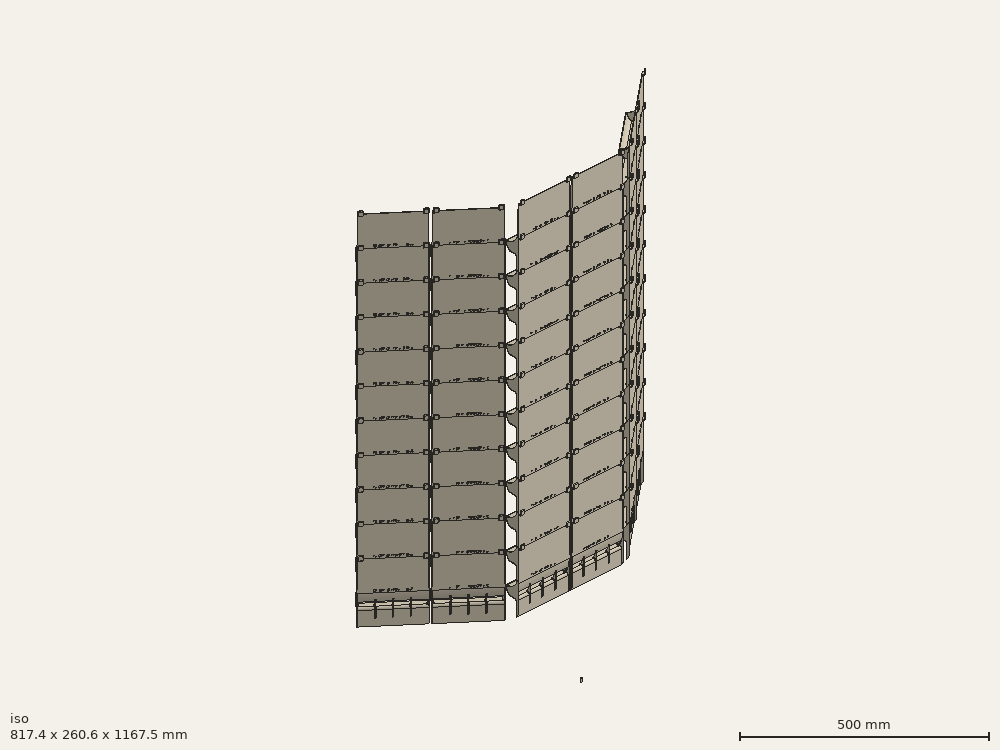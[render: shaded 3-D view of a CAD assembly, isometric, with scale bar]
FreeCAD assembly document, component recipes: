
FREECAD ASSEMBLY — COMPONENT RECIPES ("composit_stand12")

This assembly document has 30 components, labeled P0..P29 below (a component is one placed body or linked part). 28 of them carry a construction recipe — the FreeCAD feature program that regenerates the part from scratch, quoted from this document or its linked companion documents; the rest are supplied as boundary geometry only. No exploded tour is included for this assembly.
COMPONENT P0 — recipe-attached ("Body003", modeled in this document).
Construction recipe (the document's own serialized feature program — sketch geometry with constraints, then the solid features built on it; lengths are millimeters unless a unit is written):

FEATURE [PartDesign::SubShapeBinder] Binder007
  BindCopyOnChange = 0
  BindMode = 0
  ClaimChildren = false
  Context = -> Body003 [Binder007.]
  Fuse = false
  MakeFace = true
  OffsetFill = false
  OffsetIntersection = false
  OffsetJoinType = 0
  OffsetOpenResult = false
  PartialLoad = false
  Relative = true
  Support = -> [Sketch003[Edge1]]
  _Version = 2
FEATURE [Sketcher::SketchObject] Sketch016
  AttachmentSupport = -> [YZ_Plane003]
  ExternalGeometry = -> [Binder007]
  FullyConstrained = true
  MapMode = 5
  Placement = pos=(0,0,0) rot=(0.57735,0.57735,0.57735;2.0944rad)
  sketch-geometry (3):
    g0: ArcOfCircle CenterX=2.5 CenterY=3.01366 CenterZ=0 NormalX=0 NormalY=0 NormalZ=1 AngleXU=0 Radius=2.5 StartAngle=3.14159 EndAngle=4.89818
    g1: LineSegment StartX=2.9618 StartY=0.556683 StartZ=0 EndX=2.5 EndY=3.01366 EndZ=0
    g2: LineSegment StartX=2.5 StartY=3.01366 StartZ=0 EndX=0 EndY=3.01366 EndZ=0
  constraints (9):
    c: PointOnObject(g0,g-3)
    c: PointOnObject(g0,g-2)
    c: Coincident(g0,g1)
    c: Coincident(g1,g0)
    c: Coincident(g1,g2)
    c: Coincident(g2,g0)
    c: Perpendicular(g-3,g1)
    c: Perpendicular(g-2,g2)
    c: Radius(g0) = 2.5
FEATURE [PartDesign::Pad] Pad007
  Direction = (1,0,0)
  Length = 50
  Length2 = 10
  Midplane = true
  Placement = pos=(0,0,0) rot=(0.57735,0.57735,0.57735;2.0944rad)
  Profile = -> Sketch016
  ReferenceAxis = -> Sketch016 [N_Axis]
  Suppressed = false
  Type = 0
FEATURE [Sketcher::SketchObject] Sketch017
  AttachmentSupport = -> [XZ_Plane003]
  ExternalGeometry = -> [Sketch016]
  FullyConstrained = true
  MapMode = 5
  Placement = pos=(0,0,0) rot=(1,0,0;1.5708rad)
  expr: Constraints[8] = <<Pad007>>.Length
  sketch-geometry (4):
    g0: LineSegment StartX=-25 StartY=3.01366 StartZ=0 EndX=25 EndY=3.01366 EndZ=0
    g1: ArcOfCircle CenterX=23 CenterY=3.01366 CenterZ=0 NormalX=0 NormalY=0 NormalZ=1 AngleXU=0 Radius=2 StartAngle=0 EndAngle=1.5708
    g2: ArcOfCircle CenterX=-23 CenterY=3.01366 CenterZ=0 NormalX=0 NormalY=0 NormalZ=1 AngleXU=0 Radius=2 StartAngle=1.5708 EndAngle=3.14159
    g3: LineSegment StartX=-23 StartY=5.01366 StartZ=0 EndX=23 EndY=5.01366 EndZ=0
  constraints (11):
    c: PointOnObject(g1,g0)
    c: Coincident(g1,g0)
    c: PointOnObject(g2,g0)
    c: Coincident(g2,g0)
    c: Horizontal(g3)
    c: Tangent(g3,g2) = 1.5708
    c: Tangent(g3,g1) = 1.5708
    c: Symmetric(g0,g0,g-2)
    c: DistanceX(g0,g0) = 50
    c: Radius(g1) = 2
    c: PointOnObject(g-3,g0)
FEATURE [PartDesign::Pad] Pad008
  BaseFeature = -> Pad007
  Direction = (0,-1,2e-16)
  Length = 2
  Length2 = 10
  Placement = pos=(0,0,0) rot=(0.57735,0.57735,0.57735;2.0944rad)
  Profile = -> Sketch017
  ReferenceAxis = -> Sketch017 [N_Axis]
  Reversed = true
  Suppressed = false
  Type = 0
FEATURE [Sketcher::SketchObject] Sketch018
  AttachmentSupport = -> [Sketch016]
  FullyConstrained = true
  MapMode = 7
  Placement = pos=(0,2.9618,0.556683) rot=(1,0,0;0.185787rad)
  expr: Constraints[6] = <<Pad007>>.Length
  sketch-geometry (4):
    g0: ArcOfCircle CenterX=22 CenterY=0 CenterZ=0 NormalX=0 NormalY=0 NormalZ=1 AngleXU=0 Radius=3 StartAngle=0 EndAngle=1.5708
    g1: ArcOfCircle CenterX=-22 CenterY=0 CenterZ=0 NormalX=0 NormalY=0 NormalZ=1 AngleXU=0 Radius=3 StartAngle=1.5708 EndAngle=3.14159
    g2: LineSegment StartX=-22 StartY=3 StartZ=0 EndX=22 EndY=3 EndZ=0
    g3: LineSegment StartX=-25 StartY=4e-16 StartZ=0 EndX=25 EndY=0 EndZ=0
  constraints (11):
    c: PointOnObject(g0,g-1)
    c: PointOnObject(g0,g-1)
    c: PointOnObject(g1,g-1)
    c: Coincident(g3,g1)
    c: Coincident(g3,g0)
    c: Symmetric(g1,g0,g-2)
    c: DistanceX(g3,g3) = 50
    c: Horizontal(g2)
    c: Tangent(g2,g0) = 1.5708
    c: Tangent(g2,g1) = 1.5708
    c: Radius(g0) = 3
FEATURE [PartDesign::Pad] Pad009
  BaseFeature = -> Pad008
  Direction = (0,-0.18472,0.982791)
  Length = 2
  Length2 = 10
  Placement = pos=(0,0,0) rot=(0.57735,0.57735,0.57735;2.0944rad)
  Profile = -> Sketch018
  ReferenceAxis = -> Sketch018 [N_Axis]
  Suppressed = false
  Type = 0
FEATURE [PartDesign::Body] Body003
  Group = -> [Binder007,Sketch016,Pad007,Sketch017,Pad008,Sketch018,Pad009]
  Origin = -> Origin003
  Tip = -> Pad009
COMPONENT P1 — recipe-attached ("dropper_fix_composit", modeled in this document).
Construction recipe (the document's own serialized feature program — sketch geometry with constraints, then the solid features built on it; lengths are millimeters unless a unit is written):

FEATURE [PartDesign::SubShapeBinder] Binder008
  BindCopyOnChange = 0
  BindMode = 0
  ClaimChildren = true
  Context = -> Body004 [Binder008.]
  Fuse = false
  MakeFace = true
  OffsetFill = false
  OffsetIntersection = false
  OffsetJoinType = 0
  OffsetOpenResult = false
  PartialLoad = false
  Relative = true
  Support = -> [Connect002]
  _Version = 2
FEATURE [PartDesign::FeaturePython] BaseBend001  # WARN: FeaturePython — macro-defined, semantics opaque (R4)
  BendSide = 0
  BendSketch = -> Binder008
  MidPlane = false
  Reverse = false
  Suppressed = false
  length = 100
  radius = 0.1
  thickness = 0.3
FEATURE [PartDesign::FeaturePython] Extend001  # WARN: FeaturePython — macro-defined, semantics opaque (R4)
  BaseFeature = -> BaseBend001
  Offset = 0.02
  Refine = true
  Suppressed = false
  UseSubtraction = false
  baseObject = -> BaseBend001 [Face1]
  gap1 = 0
  gap2 = 0
  length = 0
FEATURE [PartDesign::FeaturePython] Bend001  # WARN: FeaturePython — macro-defined, semantics opaque (R4)
  AutoMiter = false
  BaseFeature = -> Extend001
  BendType = 1
  LengthList = [20]
  LengthSpec = 1
  ReliefFactor = 0.7
  Suppressed = false
  UseReliefFactor = false
  angle = 90
  baseObject = -> Extend001 [Edge4,Edge7,Edge14,Edge16,Edge17,Edge18]
  bendAList = [90]
  extend1 = 0
  extend2 = 0
  gap1 = 0
  gap2 = 0
  invert = false
  kfactor = 0.5
  length = 20
  maxExtendDist = 5
  minGap = 0.2
  minReliefGap = 1
  miterangle1 = 0
  miterangle2 = 0
  offset = 0
  radius = 0.1
  reliefType = 0
  reliefd = 1
  reliefw = 0.8
  sketchflip = false
  sketchinvert = false
  unfold = false
  expr: radius = BaseBend001.radius
FEATURE [PartDesign::Boolean] Boolean003
  BaseFeature = -> Bend001
  Group = -> [Fusion004]
  Suppressed = false
  Type = 1
  UsePlacement = true
FEATURE [PartDesign::Boolean] Boolean004
  BaseFeature = -> Boolean003
  Group = -> [Compound005]
  Refine = true
  Suppressed = false
  Type = 0
  UsePlacement = true
FEATURE [PartDesign::CoordinateSystem] Local_CS002  label="dropper_fix_composit_LCS"
  AttacherType = Attacher::AttachEngine3D
  AttachmentSupport = -> [XY_Plane004]
  MapMode = 5
FEATURE [PartDesign::CoordinateSystem] Local_CS003  label="dropper_fix_composit_dropper_fix_PP1_LCS"
  AttacherType = Attacher::AttachEngine3D
  AttachmentOffset = pos=(0,0,3) rot=(0,0,1;0rad)
  AttachmentSupport = -> [XY_Plane004]
  MapMode = 5
  Placement = pos=(0,0,3) rot=(0,0,1;0rad)
FEATURE [PartDesign::CoordinateSystem] Local_CS031  label="dropper_fix_composit_dropper_fix_PP2_LCS"
  AttacherType = Attacher::AttachEngine3D
  AttachmentOffset = pos=(291.934,105.683,3) rot=(0,0,1;0.694667rad)
  AttachmentSupport = -> [XY_Plane004]
  MapMode = 5
  Placement = pos=(291.934,105.683,3) rot=(0,0,1;0.694667rad)
  expr: AttachmentOffset = <<dropper_fix_composit_dropper_fix_PP1_LCS>>.AttachmentOffset * <<Placment036>>.Placement
FEATURE [PartDesign::CoordinateSystem] Local_CS032  label="dropper_fix_composit_dropper_fix_PP3_LCS"
  AttacherType = Attacher::AttachEngine3D
  AttachmentOffset = pos=(-291.934,105.683,3) rot=(0,0,1;5.58852rad)
  AttachmentSupport = -> [XY_Plane004]
  MapMode = 5
  Placement = pos=(-291.934,105.683,3) rot=(0,0,1;5.58852rad)
  expr: AttachmentOffset = <<dropper_fix_composit_dropper_fix_PP1_LCS>>.AttachmentOffset * <<Placment037>>.Placement
FEATURE [PartDesign::CoordinateSystem] Local_CS034  label="dropper_fix_composit_door_jumb_LCS"
  AttacherType = Attacher::AttachEngine3D
  AttachmentOffset = pos=(0,193,0) rot=(0,1,0;3.14159rad)
  AttachmentSupport = -> [XY_Plane004]
  MapMode = 5
  Placement = pos=(0,193,0) rot=(0,1,0;3.14159rad)
  expr: AttachmentOffset = <<door_jumb_placement>>.Placement
FEATURE [PartDesign::Boolean] Boolean006
  BaseFeature = -> Boolean004
  Group = -> [Fusion006]
  Suppressed = false
  Type = 1
  UsePlacement = true
FEATURE [PartDesign::Body] Body004  label="dropper_fix_composit"
  Group = -> [Binder008,BaseBend001,Extend001,Bend001,Boolean003,Boolean004,Boolean006,Local_CS002,Local_CS003,Local_CS031,Local_CS032,Local_CS034]
  Origin = -> Origin004
  Tip = -> Boolean006
COMPONENT P2 — recipe-attached ("dropper_fix_PP", modeled in this document).
Construction recipe (the document's own serialized feature program — sketch geometry with constraints, then the solid features built on it; lengths are millimeters unless a unit is written):

FEATURE [PartDesign::SubShapeBinder] Binder009
  BindCopyOnChange = 0
  BindMode = 0
  ClaimChildren = true
  Context = -> Body005 [Binder009.]
  Fuse = false
  MakeFace = true
  OffsetFill = false
  OffsetIntersection = false
  OffsetJoinType = 0
  OffsetOpenResult = false
  PartialLoad = false
  Relative = false
  Support = -> [Connect003]
  _Version = 2
FEATURE [PartDesign::Pad] Pad010
  Direction = (0,0,1)
  Length = 5
  Length2 = 10
  Profile = -> Binder009
  Refine = true
  Suppressed = false
  Type = 0
FEATURE [PartDesign::Boolean] Boolean005
  BaseFeature = -> Pad010
  Group = -> [Compound007]
  Suppressed = false
  Type = 1
  UsePlacement = true
FEATURE [PartDesign::CoordinateSystem] Local_CS001  label="dropper_fix_PP_LCS"
  AttacherType = Attacher::AttachEngine3D
  AttachmentSupport = -> [XY_Plane005]
  MapMode = 5
FEATURE [PartDesign::Body] Body005  label="dropper_fix_PP"
  Group = -> [Binder009,Pad010,Boolean005,Local_CS001]
  Origin = -> Origin005
  Tip = -> Boolean005
COMPONENT P3 — recipe-attached ("bar", modeled in this document).
Construction recipe (the document's own serialized feature program — sketch geometry with constraints, then the solid features built on it; lengths are millimeters unless a unit is written):

FEATURE [PartDesign::SubShapeBinder] Binder012
  BindCopyOnChange = 0
  BindMode = 0
  ClaimChildren = true
  Context = -> Body006 [Binder012.]
  Fuse = false
  MakeFace = true
  OffsetFill = false
  OffsetIntersection = false
  OffsetJoinType = 0
  OffsetOpenResult = false
  PartialLoad = false
  Relative = false
  Support = -> [Connect004]
  _Version = 2
FEATURE [PartDesign::FeaturePython] BaseBend008  label="bar_BaseBend"  # WARN: FeaturePython — macro-defined, semantics opaque (R4)
  BendSide = 1
  BendSketch = -> Binder012
  MidPlane = true
  Reverse = false
  Suppressed = false
  length = 888.273
  radius = 2
  thickness = 2
  expr: length = <<Dimensions>>.Constraints.width - 6 mm
  expr: thickness = <<bar_sketch>>.Constraints.thickness
FEATURE [Sketcher::SketchObject] Sketch049
  AttachmentOffset = pos=(32.5,444.137,0) rot=(0,0,1;0rad)
  AttachmentSupport = -> [XZ_Plane007]
  FullyConstrained = true
  MapMode = 5
  Placement = pos=(32.5,9.86e-14,444.137) rot=(1,0,0;1.5708rad)
  expr: .AttachmentOffset.Base.x = <<bar_sketch>>.Constraints.total_width / 2
  expr: .AttachmentOffset.Base.y = <<bar_BaseBend>>.length / 2
  sketch-geometry (3):
    g0: ArcOfCircle CenterX=-5 CenterY=-5 CenterZ=0 NormalX=0 NormalY=0 NormalZ=1 AngleXU=0 Radius=5 StartAngle=-2.7e-15 EndAngle=1.5708
    g1: LineSegment StartX=0 StartY=-5 StartZ=0 EndX=0 EndY=0 EndZ=0
    g2: LineSegment StartX=0 StartY=0 StartZ=0 EndX=-5 EndY=0 EndZ=0
  constraints (7):
    c: PointOnObject(g0,g-2)
    c: PointOnObject(g0,g-1)
    c: Coincident(g1,g2)
    c: Tangent(g0,g1) = -1.5708
    c: Tangent(g2,g0) = -1.5708
    c: Coincident(g1,g-1)
    c: Radius(g0) = 5
FEATURE [PartDesign::Pocket] Pocket005
  BaseFeature = -> BaseBend008
  Direction = (0,1,-2e-16)
  Length = 5
  Length2 = 5
  Midplane = true
  Profile = -> Sketch049
  ReferenceAxis = -> Sketch049 [N_Axis]
  Refine = true
  Suppressed = false
  Type = 1
FEATURE [PartDesign::Mirrored] Mirrored001
  MirrorPlane = -> YZ_Plane007
  Suppressed = false
FEATURE [PartDesign::Mirrored] Mirrored002
  MirrorPlane = -> XY_Plane007
  Suppressed = false
FEATURE [PartDesign::MultiTransform] MultiTransform
  BaseFeature = -> Pocket005
  Originals = -> [Pocket005]
  Suppressed = false
  Transformations = -> [Mirrored001,Mirrored002]
FEATURE [PartDesign::CoordinateSystem] Local_CS008  label="bar_LCS"
  AttacherType = Attacher::AttachEngine3D
  AttachmentSupport = -> [XY_Plane007]
  MapMode = 5
FEATURE [PartDesign::CoordinateSystem] Local_CS009  label="bar_bar_fix_LCS"
  AttacherType = Attacher::AttachEngine3D
  AttachmentOffset = pos=(0,25,-444.137) rot=(0,0,1;3.14159rad)
  AttachmentSupport = -> [XY_Plane007]
  MapMode = 5
  Placement = pos=(0,25,-444.137) rot=(0,0,1;3.14159rad)
  expr: AttachmentOffset = <<bar_fix_placement>>.Placement
FEATURE [PartDesign::CoordinateSystem] Local_CS010  label="bar_bar_fix2_LCS"
  AttacherType = Attacher::AttachEngine3D
  AttachmentOffset = pos=(0,25,444.137) rot=(1,0,0;3.14159rad)
  AttachmentSupport = -> [XY_Plane007]
  MapMode = 5
  Placement = pos=(0,25,444.137) rot=(1,0,0;3.14159rad)
  expr: .AttachmentOffset.Base.y = <<bar_bar_fix_LCS>>.AttachmentOffset.Base.y
  expr: .AttachmentOffset.Base.z = -<<bar_bar_fix_LCS>>.AttachmentOffset.Base.z
FEATURE [Sketcher::SketchObject] Sketch073
  AttachmentOffset = pos=(17.5,-215,0) rot=(0,0,1;0rad)
  AttachmentSupport = -> [XZ_Plane007]
  FullyConstrained = true
  MapMode = 5
  Placement = pos=(17.5,-4.77e-14,-215) rot=(1,0,0;1.5708rad)
  expr: .AttachmentOffset.Base.x = <<bar_sketch>>.Constraints.inner / 2
  sketch-geometry (7):
    g0: LineSegment StartX=-2 StartY=50 StartZ=0 EndX=2.7 EndY=50 EndZ=0
    g1: ArcOfCircle CenterX=-2 CenterY=48 CenterZ=0 NormalX=0 NormalY=0 NormalZ=1 AngleXU=0 Radius=2 StartAngle=1.5708 EndAngle=3.14159
    g2: ArcOfCircle CenterX=2.7 CenterY=48 CenterZ=0 NormalX=0 NormalY=0 NormalZ=1 AngleXU=0 Radius=2 StartAngle=4e-16 EndAngle=1.5708
    g3: LineSegment StartX=-4 StartY=48 StartZ=0 EndX=-4 EndY=0 EndZ=0
    g4: LineSegment StartX=-4 StartY=0 StartZ=0 EndX=4.7 EndY=0 EndZ=0
    g5: LineSegment StartX=4.7 StartY=0 StartZ=0 EndX=4.7 EndY=48 EndZ=0
    g6: GeomPoint X=0 Y=50 Z=0
  constraints (18):
    c: Horizontal(g0)
    c: DistanceX(g0) = -2
    c: DistanceX(g0) = 2.7
    c: Tangent(g1,g3) = -1.5708
    c: Coincident(g3,g4)
    c: PointOnObject(g4,g-1)
    c: Horizontal(g4)
    c: Coincident(g4,g5)
    c: Vertical(g5)
    c: Tangent(g5,g2) = -1.5708
    c: Vertical(g3)
    c: Equal(g2,g1)
    c: Radius(g2) = 2
    c: Tangent(g2,g0) = 1.5708
    c: Tangent(g1,g0) = 1.5708
    c: PointOnObject(g6,g-2)
    c: DistanceY(g6) = 50
    c: PointOnObject(g6,g0)
FEATURE [PartDesign::Mirrored] Mirrored005
  MirrorPlane = -> Sketch073 [H_Axis]
  Suppressed = false
FEATURE [PartDesign::Mirrored] Mirrored006
  MirrorPlane = -> XY_Plane007
  Suppressed = false
FEATURE [PartDesign::Boolean] Boolean007
  BaseFeature = -> MultiTransform
  Group = -> [Fusion010]
  Suppressed = false
  Type = 1
  UsePlacement = true
FEATURE [PartDesign::Pocket] Pocket010
  BaseFeature = -> Boolean007
  Direction = (0,1,-2e-16)
  Length = 5
  Length2 = 5
  Profile = -> Sketch073
  ReferenceAxis = -> Sketch073 [N_Axis]
  Suppressed = false
  Type = 1
FEATURE [PartDesign::MultiTransform] MultiTransform001
  BaseFeature = -> Pocket010
  Originals = -> [Pocket010]
  Suppressed = false
  Transformations = -> [Mirrored005,Mirrored006]
FEATURE [PartDesign::Body] Body006  label="bar"
  Group = -> [Binder012,BaseBend008,Sketch049,Pocket005,MultiTransform,Mirrored001,Mirrored002,Boolean007,Local_CS008,Local_CS009,Local_CS010,Sketch073,Pocket010,MultiTransform001,Mirrored005,Mirrored006]
  Origin = -> Origin007
  Tip = -> MultiTransform001
COMPONENT P4 — recipe-attached ("bar_fix", modeled in this document).
Construction recipe (the document's own serialized feature program — sketch geometry with constraints, then the solid features built on it; lengths are millimeters unless a unit is written):

FEATURE [PartDesign::SubShapeBinder] Binder013
  BindCopyOnChange = 0
  BindMode = 0
  ClaimChildren = true
  Context = -> Body008 [Binder013.]
  Fuse = false
  MakeFace = true
  OffsetFill = false
  OffsetIntersection = false
  OffsetJoinType = 0
  OffsetOpenResult = false
  PartialLoad = false
  Placement = pos=(0,0,0) rot=(0.57735,0.57735,0.57735;2.0944rad)
  Relative = false
  Support = -> [Sketch050]
  _Version = 2
FEATURE [PartDesign::FeaturePython] BaseBend009  # WARN: FeaturePython — macro-defined, semantics opaque (R4)
  BendSide = 1
  BendSketch = -> Binder013
  MidPlane = true
  Reverse = false
  Suppressed = false
  length = 31
  radius = 2
  thickness = 2
  expr: length = <<bar_sketch>>.Constraints.inner - 4 mm
FEATURE [Sketcher::SketchObject] Sketch051
  AttachmentOffset = pos=(15.5,34,0) rot=(0,0,1;0rad)
  AttachmentSupport = -> [XZ_Plane009]
  FullyConstrained = true
  MapMode = 5
  Placement = pos=(15.5,7.5e-15,34) rot=(1,0,0;1.5708rad)
  expr: .AttachmentOffset.Base.x = <<BaseBend009>>.length / 2
  expr: .AttachmentOffset.Base.y = <<Sketch050>>.Constraints.bar1
  sketch-geometry (3):
    g0: ArcOfCircle CenterX=-5 CenterY=-5 CenterZ=0 NormalX=0 NormalY=0 NormalZ=1 AngleXU=0 Radius=5 StartAngle=2.886e-13 EndAngle=1.5708
    g1: LineSegment StartX=-5.68e-14 StartY=-5 StartZ=0 EndX=-5.68e-14 EndY=-5.68e-14 EndZ=0
    g2: LineSegment StartX=-5.68e-14 StartY=-5.68e-14 StartZ=0 EndX=-5 EndY=-5.68e-14 EndZ=0
  constraints (8):
    c: PointOnObject(g0,g-2)
    c: PointOnObject(g0,g-1)
    c: Coincident(g1,g2)
    c: Horizontal(g2)
    c: Tangent(g2,g0) = -1.5708
    c: Tangent(g0,g1) = -1.5708
    c: Vertical(g1)
    c: Radius(g0) = 5
FEATURE [PartDesign::Pocket] Pocket006
  BaseFeature = -> BaseBend009
  Direction = (0,1,-2e-16)
  Length = 5
  Length2 = 5
  Profile = -> Sketch051
  ReferenceAxis = -> Sketch051 [N_Axis]
  Suppressed = false
  Type = 0
FEATURE [Sketcher::SketchObject] Sketch052
  AttachmentOffset = pos=(15.5,29,0) rot=(0,0,1;0rad)
  AttachmentSupport = -> [XY_Plane009]
  FullyConstrained = true
  MapMode = 5
  Placement = pos=(15.5,29,0) rot=(0,0,1;0rad)
  expr: .AttachmentOffset.Base.x = <<BaseBend009>>.length / 2
  expr: .AttachmentOffset.Base.y = <<Sketch050>>.Constraints.wall
  sketch-geometry (3):
    g0: ArcOfCircle CenterX=-5 CenterY=-5 CenterZ=0 NormalX=0 NormalY=0 NormalZ=1 AngleXU=0 Radius=5 StartAngle=0 EndAngle=1.5708
    g1: LineSegment StartX=0 StartY=-5 StartZ=0 EndX=0 EndY=0 EndZ=0
    g2: LineSegment StartX=0 StartY=0 StartZ=0 EndX=-5 EndY=0 EndZ=0
  constraints (8):
    c: PointOnObject(g0,g-2)
    c: PointOnObject(g0,g-1)
    c: Coincident(g1,g2)
    c: Vertical(g1)
    c: Horizontal(g2)
    c: Tangent(g0,g1) = -1.5708
    c: Tangent(g2,g0) = -1.5708
    c: Radius(g0) = 5
FEATURE [PartDesign::Pocket] Pocket007
  BaseFeature = -> Pocket006
  Direction = (0,0,-1)
  Length = 5
  Length2 = 5
  Midplane = true
  Profile = -> Sketch052
  ReferenceAxis = -> Sketch052 [N_Axis]
  Suppressed = false
  Type = 0
FEATURE [PartDesign::Mirrored] Mirrored003
  BaseFeature = -> Pocket007
  MirrorPlane = -> YZ_Plane009
  Originals = -> [Pocket006,Pocket007]
  Suppressed = false
FEATURE [PartDesign::Boolean] Boolean008
  BaseFeature = -> Mirrored003
  Group = -> [Fusion011]
  Suppressed = false
  Type = 1
  UsePlacement = true
FEATURE [PartDesign::CoordinateSystem] Local_CS013  label="bar_fix_LCS"
  AttacherType = Attacher::AttachEngine3D
  AttachmentSupport = -> [XY_Plane009]
  MapMode = 5
FEATURE [PartDesign::Body] Body008  label="bar_fix"
  Group = -> [Binder013,BaseBend009,Sketch051,Pocket006,Sketch052,Pocket007,Mirrored003,Boolean008,Local_CS013]
  Origin = -> Origin009
  Tip = -> Boolean008
COMPONENT P5 — recipe-attached ("pan", modeled in this document).
Construction recipe (the document's own serialized feature program — sketch geometry with constraints, then the solid features built on it; lengths are millimeters unless a unit is written):

FEATURE [PartDesign::SubShapeBinder] Binder014
  BindCopyOnChange = 0
  BindMode = 0
  ClaimChildren = true
  Context = -> Body009 [Binder014.]
  Fuse = false
  MakeFace = true
  OffsetFill = false
  OffsetIntersection = false
  OffsetJoinType = 0
  OffsetOpenResult = false
  PartialLoad = false
  Relative = true
  Support = -> [Sketch055]
  _Version = 2
FEATURE [PartDesign::FeaturePython] BaseBend010  # WARN: FeaturePython — macro-defined, semantics opaque (R4)
  BendSide = 0
  BendSketch = -> Binder014
  MidPlane = false
  Reverse = false
  Suppressed = false
  length = 100
  radius = 0.1
  thickness = 0.3
FEATURE [PartDesign::FeaturePython] Bend002  # WARN: FeaturePython — macro-defined, semantics opaque (R4)
  AutoMiter = false
  BaseFeature = -> BaseBend010
  BendType = 1
  LengthList = [40]
  LengthSpec = 1
  ReliefFactor = 0.7
  Suppressed = false
  UseReliefFactor = false
  angle = 90
  baseObject = -> BaseBend010 [Edge4,Edge7,Edge10,Edge12]
  bendAList = [90]
  extend1 = 0
  extend2 = 0
  gap1 = 0
  gap2 = 0
  invert = false
  kfactor = 0.5
  length = 40
  maxExtendDist = 5
  minGap = 0.2
  minReliefGap = 1
  miterangle1 = 0
  miterangle2 = 0
  offset = 0
  radius = 0.1
  reliefType = 0
  reliefd = 1
  reliefw = 0.8
  sketchflip = false
  sketchinvert = false
  unfold = false
  expr: radius = BaseBend010.radius
FEATURE [PartDesign::CoordinateSystem] Local_CS016  label="pan_LCS"
  AttacherType = Attacher::AttachEngine3D
  AttachmentSupport = -> [XY_Plane010]
  MapMode = 5
FEATURE [PartDesign::CoordinateSystem] Local_CS023  label="pan_basin_LCS"
  AttacherType = Attacher::AttachEngine3D
  AttachmentOffset = pos=(0,120,3) rot=(0,0,1;0rad)
  AttachmentSupport = -> [XY_Plane010]
  MapMode = 5
  Placement = pos=(0,120,3) rot=(0,0,1;0rad)
FEATURE [Sketcher::SketchObject] Sketch071
  AttachmentOffset = pos=(0,0,-255) rot=(0,0,1;0rad)
  AttachmentSupport = -> [XZ_Plane010]
  FullyConstrained = true
  MapMode = 5
  Placement = pos=(0,255,-5.66e-14) rot=(1,0,0;1.5708rad)
  expr: .AttachmentOffset.Base.z = -<<pan_base_Sketch>>.Constraints.depth
  expr: Constraints[6] = <<pan_base_Sketch>>.Constraints.width / 2 - 0.4 mm
  sketch-geometry (8):
    g0: LineSegment StartX=-431.737 StartY=70 StartZ=0 EndX=431.737 EndY=70 EndZ=0
    g1: LineSegment StartX=428.737 StartY=0.4 StartZ=0 EndX=-428.737 EndY=0.4 EndZ=0
    g2: LineSegment StartX=428.737 StartY=43.2 StartZ=0 EndX=428.737 EndY=0.4 EndZ=0
    g3: LineSegment StartX=431.737 StartY=70 StartZ=0 EndX=431.737 EndY=43.2 EndZ=0
    g4: LineSegment StartX=431.737 StartY=43.2 StartZ=0 EndX=428.737 EndY=43.2 EndZ=0
    g5: LineSegment StartX=-428.737 StartY=0.4 StartZ=0 EndX=-428.737 EndY=43.2 EndZ=0
    g6: LineSegment StartX=-428.737 StartY=43.2 StartZ=0 EndX=-431.737 EndY=43.2 EndZ=0
    g7: LineSegment StartX=-431.737 StartY=43.2 StartZ=0 EndX=-431.737 EndY=70 EndZ=0
  constraints (22):
    c: Coincident(g7,g0)
    c: Coincident(g0,g3)
    c: Coincident(g2,g1)
    c: Coincident(g1,g5)
    c: Horizontal(g0)
    c: DistanceY(g0) = 70  'height'
    c: DistanceX(g2) = 428.737
    c: DistanceY(g2) = 0.4
    c: Coincident(g4,g2)
    c: Vertical(g2)
    c: Coincident(g3,g4)
    c: Vertical(g3)
    c: Coincident(g5,g6)
    c: Vertical(g5)
    c: Coincident(g6,g7)
    c: Vertical(g7)
    c: Horizontal(g6)
    c: Horizontal(g4)
    c: Symmetric(g1,g1,g-2)
    c: Symmetric(g3,g6,g-2)
    c: DistanceX(g4,g4) = 3
    c: DistanceY(g2) = 43.2
FEATURE [PartDesign::Pad] Pad015
  BaseFeature = -> Bend002
  Direction = (0,-1,2e-16)
  Length = 0.3
  Length2 = 10
  Profile = -> Sketch071
  ReferenceAxis = -> Sketch071 [N_Axis]
  Refine = true
  Suppressed = false
  Type = 0
FEATURE [PartDesign::FeaturePython] Bend005  # WARN: FeaturePython — macro-defined, semantics opaque (R4)
  AutoMiter = true
  BaseFeature = -> Pad015
  BendType = 0
  LengthList = [3]
  LengthSpec = 1
  ReliefFactor = 0.7
  Suppressed = false
  UseReliefFactor = false
  angle = 90
  baseObject = -> Pad015 [Edge7,Edge10]
  bendAList = [90]
  extend1 = 0
  extend2 = 0
  gap1 = 0
  gap2 = 0
  invert = false
  kfactor = 0.5
  length = 3
  maxExtendDist = 5
  minGap = 0.2
  minReliefGap = 1
  miterangle1 = 0
  miterangle2 = 0
  offset = 0
  radius = 0.1
  reliefType = 0
  reliefd = 1
  reliefw = 0.8
  sketchflip = false
  sketchinvert = false
  unfold = false
  expr: radius = BaseBend010.radius
FEATURE [Sketcher::SketchObject] Sketch072
  AttachmentOffset = pos=(0,0,429.137) rot=(0,0,1;0rad)
  AttachmentSupport = -> [YZ_Plane010]
  ExternalGeometry = -> [Binder014]
  FullyConstrained = true
  MapMode = 5
  Placement = pos=(429.137,0,0) rot=(0.57735,0.57735,0.57735;2.0944rad)
  expr: .AttachmentOffset.Base.z = <<pan_base_Sketch>>.Constraints.width / 2
  sketch-geometry (8):
    g0: LineSegment StartX=0 StartY=0 StartZ=0 EndX=3 EndY=0 EndZ=0
    g1: LineSegment StartX=3 StartY=0 StartZ=0 EndX=3 EndY=40 EndZ=0
    g2: LineSegment StartX=3 StartY=40 StartZ=0 EndX=0 EndY=40 EndZ=0
    g3: LineSegment StartX=0 StartY=40 StartZ=0 EndX=0 EndY=0 EndZ=0
    g4: LineSegment StartX=255 StartY=0 StartZ=0 EndX=255 EndY=40 EndZ=0
    g5: LineSegment StartX=255 StartY=40 StartZ=0 EndX=251.7 EndY=40 EndZ=0
    g6: LineSegment StartX=251.7 StartY=40 StartZ=0 EndX=251.7 EndY=0 EndZ=0
    g7: LineSegment StartX=251.7 StartY=0 StartZ=0 EndX=255 EndY=0 EndZ=0
  constraints (22):
    c: Coincident(g0,g1)
    c: Coincident(g1,g2)
    c: Coincident(g2,g3)
    c: Coincident(g3,g0)
    c: Horizontal(g0)
    c: Horizontal(g2)
    c: Vertical(g1)
    c: Vertical(g3)
    c: Coincident(g0,g-3)
    c: Coincident(g4,g5)
    c: Coincident(g5,g6)
    c: Coincident(g6,g7)
    c: Coincident(g7,g4)
    c: Vertical(g4)
    c: Vertical(g6)
    c: Horizontal(g5)
    c: Horizontal(g7)
    c: Coincident(g4,g-3)
    c: DistanceX(g7,g7) = 3.3
    c: DistanceY(g4) = 40
    c: Equal(g6,g1)
    c: DistanceX(g0,g0) = 3
FEATURE [PartDesign::Pocket] Pocket009
  BaseFeature = -> Bend005
  Direction = (-1,0,0)
  Length = 0.4
  Length2 = 5
  Profile = -> Sketch072
  ReferenceAxis = -> Sketch072 [N_Axis]
  Suppressed = false
  Type = 0
FEATURE [PartDesign::Mirrored] Mirrored008
  BaseFeature = -> Pocket009
  MirrorPlane = -> YZ_Plane010
  Originals = -> [Pocket009]
  Suppressed = false
FEATURE [Sketcher::SketchObject] Sketch078
  AttachmentSupport = -> [Sketch072]
  ExternalGeometry = -> [Binder014]
  FullyConstrained = true
  MapMode = 5
  Placement = pos=(429.137,0,0) rot=(0.57735,0.57735,0.57735;2.0944rad)
  sketch-geometry (4):
    g0: LineSegment StartX=251.7 StartY=0.4 StartZ=0 EndX=251.7 EndY=55 EndZ=0
    g1: LineSegment StartX=151.7 StartY=0.4 StartZ=0 EndX=251.7 EndY=0.4 EndZ=0
    g2: LineSegment StartX=251.7 StartY=55 StartZ=0 EndX=151.7 EndY=55 EndZ=0
    g3: LineSegment StartX=151.7 StartY=55 StartZ=0 EndX=151.7 EndY=0.4 EndZ=0
  constraints (12):
    c: Vertical(g0)
    c: Coincident(g0,g2)
    c: Coincident(g3,g1)
    c: Coincident(g1,g0)
    c: Horizontal(g1)
    c: DistanceX(g-3,g0) = -3.3
    c: DistanceY(g-3,g0) = 0.4
    c: DistanceY(g0) = 55
    c: Coincident(g2,g3)
    c: Horizontal(g2)
    c: Vertical(g3)
    c: DistanceX(g1,g1) = 100
FEATURE [Sketcher::SketchObject] Sketch079
  AttachmentOffset = pos=(0,0,3) rot=(0,0,1;0rad)
  AttachmentSupport = -> [Sketch072]
  ExternalGeometry = -> [Binder014]
  FullyConstrained = true
  MapMode = 5
  Placement = pos=(432.137,0,0) rot=(0.57735,0.57735,0.57735;2.0944rad)
  expr: Constraints[5] = <<Sketch071>>.Constraints.height
  sketch-geometry (4):
    g0: LineSegment StartX=252 StartY=70 StartZ=0 EndX=235 EndY=70 EndZ=0
    g1: LineSegment StartX=235 StartY=43.2 StartZ=0 EndX=252 EndY=43.2 EndZ=0
    g2: LineSegment StartX=252 StartY=43.2 StartZ=0 EndX=252 EndY=70 EndZ=0
    g3: ArcOfCircle CenterX=235 CenterY=56.6 CenterZ=0 NormalX=0 NormalY=0 NormalZ=1 AngleXU=0 Radius=13.4 StartAngle=1.5708 EndAngle=4.71239
  constraints (11):
    c: Horizontal(g1)
    c: Coincident(g1,g2)
    c: Vertical(g2)
    c: Coincident(g0,g2)
    c: DistanceX(g1,g-3) = 3
    c: DistanceY(g0) = 70
    c: DistanceY(g1) = 43.2
    c: Tangent(g0,g3) = -1.5708
    c: Tangent(g1,g3) = -1.5708
    c: Horizontal(g0)
    c: DistanceX(g3,g-3) = 20
FEATURE [PartDesign::Pad] Pad019
  BaseFeature = -> Mirrored008
  Direction = (1,0,0)
  Length = 0.3
  Length2 = 10
  Profile = -> Sketch079
  ReferenceAxis = -> Sketch079 [N_Axis]
  Reversed = true
  Suppressed = false
  Type = 0
FEATURE [PartDesign::SubShapeBinder] Binder026
  BindCopyOnChange = 0
  BindMode = 0
  ClaimChildren = true
  Context = -> <external composit_stand12_model.FCStd>#Assembly [pan.Binder026.]
  Fuse = false
  MakeFace = true
  OffsetFill = false
  OffsetIntersection = false
  OffsetJoinType = 0
  OffsetOpenResult = false
  PartialLoad = false
  Relative = false
  Support = -> [Part__Mirroring018]
  _Version = 2
FEATURE [PartDesign::Pad] Pad020
  BaseFeature = -> Pad019
  Direction = (1,0,0)
  Length = 0.3
  Length2 = 10
  Profile = -> Binder026 [Face1]
  Suppressed = false
  Type = 0
FEATURE [PartDesign::Pad] Pad021
  BaseFeature = -> Pad020
  Direction = (1,0,0)
  Length = 0.3
  Length2 = 10
  Profile = -> Sketch078
  ReferenceAxis = -> Sketch078 [N_Axis]
  Reversed = true
  Suppressed = false
  Type = 0
FEATURE [Sketcher::SketchObject] Sketch080
  AttachmentOffset = pos=(0,0,4) rot=(0,0,1;0rad)
  AttachmentSupport = -> [XY_Plane010]
  ExternalGeometry = -> [Binder014]
  FullyConstrained = true
  MapMode = 5
  Placement = pos=(0,0,4) rot=(0,0,1;0rad)
  sketch-geometry (6):
    g0: ArcOfCircle CenterX=428.737 CenterY=3 CenterZ=0 NormalX=0 NormalY=0 NormalZ=1 AngleXU=0 Radius=0.4 StartAngle=4.71239 EndAngle=6.28319
    g1: ArcOfCircle CenterX=428.737 CenterY=3 CenterZ=0 NormalX=0 NormalY=0 NormalZ=1 AngleXU=0 Radius=0.1 StartAngle=4.71239 EndAngle=6.28319
    g2: LineSegment StartX=428.837 StartY=3 StartZ=0 EndX=429.137 EndY=3 EndZ=0
    g3: LineSegment StartX=428.737 StartY=2.9 StartZ=0 EndX=399.137 EndY=2.9 EndZ=0
    g4: LineSegment StartX=399.137 StartY=2.9 StartZ=0 EndX=399.137 EndY=2.6 EndZ=0
    g5: LineSegment StartX=399.137 StartY=2.6 StartZ=0 EndX=428.737 EndY=2.6 EndZ=0
  constraints (17):
    c: PointOnObject(g0,g-3)
    c: DistanceY(g-3,g0) = 3
    c: Coincident(g1,g0)
    c: Coincident(g2,g1)
    c: Coincident(g2,g0)
    c: Horizontal(g2)
    c: Horizontal(g0,g0)
    c: Tangent(g1,g3) = 1.5708
    c: Coincident(g3,g4)
    c: Vertical(g4)
    c: Coincident(g4,g5)
    c: Horizontal(g5)
    c: Horizontal(g3)
    c: Tangent(g5,g0) = -1.5708
    c: DistanceX(g4,g-3) = 30
    c: Radius(g1) = 0.1
    c: Radius(g0) = 0.4
FEATURE [PartDesign::Pad] Pad022
  BaseFeature = -> Pad021
  Direction = (0,0,1)
  Length = 36
  Length2 = 10
  Profile = -> Sketch080
  ReferenceAxis = -> Sketch080 [N_Axis]
  Suppressed = false
  Type = 0
  expr: Length = <<Bend002>>.length - .Profile[0].Placement.Base.z * 1 mm
FEATURE [PartDesign::SubShapeBinder] Binder027
  BindCopyOnChange = 0
  BindMode = 0
  ClaimChildren = true
  Context = -> <external composit_stand12_model.FCStd>#Assembly [pan.Binder027.]
  Fuse = false
  MakeFace = true
  OffsetFill = false
  OffsetIntersection = false
  OffsetJoinType = 0
  OffsetOpenResult = false
  PartialLoad = false
  Relative = false
  Support = -> [Part__Mirroring019]
  _Version = 2
FEATURE [PartDesign::Pad] Pad023
  BaseFeature = -> Pad022
  Direction = (1,0,0)
  Length = 0.3
  Length2 = 10
  Profile = -> Binder027
  Suppressed = false
  Type = 0
FEATURE [PartDesign::SubShapeBinder] Binder028
  BindCopyOnChange = 0
  BindMode = 0
  ClaimChildren = true
  Context = -> <external composit_stand12_model.FCStd>#Assembly [pan.Binder028.]
  Fuse = false
  MakeFace = true
  OffsetFill = false
  OffsetIntersection = false
  OffsetJoinType = 0
  OffsetOpenResult = false
  PartialLoad = false
  Relative = false
  Support = -> [Part__Mirroring020]
  _Version = 2
FEATURE [PartDesign::Pad] Pad024
  BaseFeature = -> Pad023
  Direction = (0,0,1)
  Length = 36
  Length2 = 10
  Profile = -> Binder028
  Refine = true
  Suppressed = false
  Type = 0
  expr: Length = <<Pad022>>.Length
FEATURE [Sketcher::SketchObject] Sketch083
  AttachmentSupport = -> [Sketch071]
  ExternalGeometry = -> [Sketch071]
  FullyConstrained = true
  MapMode = 2
  Placement = pos=(0,255,-5.66e-14) rot=(1,0,0;1.5708rad)
  sketch-geometry (16):
    g0: LineSegment StartX=428.737 StartY=0.4 StartZ=0 EndX=435.737 EndY=0.4 EndZ=0
    g1: LineSegment StartX=437.737 StartY=2.4 StartZ=0 EndX=437.737 EndY=38 EndZ=0
    g2: LineSegment StartX=435.737 StartY=40 StartZ=0 EndX=428.737 EndY=40 EndZ=0
    g3: LineSegment StartX=428.737 StartY=0.4 StartZ=0 EndX=428.737 EndY=40 EndZ=0
    g4: ArcOfCircle CenterX=435.737 CenterY=38 CenterZ=0 NormalX=0 NormalY=0 NormalZ=1 AngleXU=0 Radius=2 StartAngle=4e-16 EndAngle=1.5708
    g5: GeomPoint X=437.737 Y=40 Z=0
    g6: ArcOfCircle CenterX=435.737 CenterY=2.4 CenterZ=0 NormalX=0 NormalY=0 NormalZ=1 AngleXU=0 Radius=2 StartAngle=4.71239 EndAngle=6.28319
    g7: GeomPoint X=437.737 Y=0.4 Z=0
    g8: LineSegment StartX=-428.737 StartY=0.4 StartZ=0 EndX=-435.737 EndY=0.4 EndZ=0
    g9: LineSegment StartX=-437.737 StartY=2.4 StartZ=0 EndX=-437.737 EndY=38 EndZ=0
    g10: LineSegment StartX=-435.737 StartY=40 StartZ=0 EndX=-428.737 EndY=40 EndZ=0
    g11: LineSegment StartX=-428.737 StartY=0.4 StartZ=0 EndX=-428.737 EndY=40 EndZ=0
    g12: ArcOfCircle CenterX=-435.737 CenterY=38 CenterZ=0 NormalX=0 NormalY=0 NormalZ=1 AngleXU=0 Radius=2 StartAngle=1.5708 EndAngle=3.14159
    g13: GeomPoint X=-437.737 Y=40 Z=0
    g14: ArcOfCircle CenterX=-435.737 CenterY=2.4 CenterZ=0 NormalX=0 NormalY=0 NormalZ=1 AngleXU=0 Radius=2 StartAngle=3.14159 EndAngle=4.71239
    g15: GeomPoint X=-437.737 Y=0.4 Z=0
  constraints (37):
    c: Horizontal(g0)
    c: Vertical(g1)
    c: Horizontal(g2)
    c: Coincident(g0,g-3)
    c: DistanceY(g2,g-3) = 3.2
    c: Coincident(g3,g0)
    c: Coincident(g3,g2)
    c: Vertical(g3)
    c: DistanceX(g2,g5) = 9
    c: PointOnObject(g5,g1)
    c: PointOnObject(g5,g2)
    c: Tangent(g1,g4) = -1.5708
    c: Tangent(g2,g4) = -1.5708
    c: PointOnObject(g7,g0)
    c: PointOnObject(g7,g1)
    c: Tangent(g0,g6) = -1.5708
    c: Tangent(g1,g6) = -1.5708
    c: Equal(g6,g4)
    c: Radius(g6) = 2
    c: Horizontal(g8)
    c: Vertical(g9)
    c: Horizontal(g10)
    c: Coincident(g11,g8)
    c: Coincident(g11,g10)
    c: Vertical(g11)
    c: PointOnObject(g13,g9)
    c: PointOnObject(g13,g10)
    c: Tangent(g9,g12) = 1.5708
    c: Tangent(g10,g12) = 1.5708
    c: PointOnObject(g15,g8)
    c: PointOnObject(g15,g9)
    c: Tangent(g8,g14) = 1.5708
    c: Tangent(g9,g14) = 1.5708
    c: Equal(g14,g12)
    c: Radius(g14) = 2
    c: Symmetric(g15,g7,g-2)
    c: Symmetric(g2,g10,g-2)
FEATURE [PartDesign::Pad] Pad025
  BaseFeature = -> Pad024
  Direction = (0,-1,2e-16)
  Length = 0.3
  Length2 = 10
  Profile = -> Sketch083
  ReferenceAxis = -> Sketch083 [N_Axis]
  Refine = true
  Suppressed = false
  Type = 0
FEATURE [PartDesign::CoordinateSystem] Local_CS035  label="pan_pan_face_LCS"
  AttacherType = Attacher::AttachEngine3D
  AttachmentOffset = pos=(2e-15,260,0) rot=(1,0,0;1.5708rad)
  AttachmentSupport = -> [XY_Plane010]
  MapMode = 5
  Placement = pos=(2e-15,260,0) rot=(1,0,0;1.5708rad)
  expr: AttachmentOffset = <<pan_face_placement>>.Placement
FEATURE [PartDesign::Boolean] Boolean009
  BaseFeature = -> Pad025
  Group = -> [Fusion012]
  Suppressed = false
  Type = 1
  UsePlacement = true
FEATURE [PartDesign::Body] Body009  label="pan"
  Group = -> [Binder014,BaseBend010,Bend002,Local_CS016,Local_CS023,Sketch071,Pad015,Bend005,Sketch072,Pocket009,Mirrored008,Sketch078,Sketch079,Pad019,Binder026,Pad020,Pad021,Sketch080,Pad022,Binder027,Pad023,Binder028,Pad024,Sketch083,Pad025,Local_CS035,Boolean009]
  Origin = -> Origin010
  Tip = -> Pad025
COMPONENT P6 — recipe-attached ("cap_outer", modeled in this document).
Construction recipe (the document's own serialized feature program — sketch geometry with constraints, then the solid features built on it; lengths are millimeters unless a unit is written):

FEATURE [PartDesign::SubShapeBinder] Binder016
  BindCopyOnChange = 0
  BindMode = 0
  ClaimChildren = true
  Context = -> Body010 [Binder016.]
  Fuse = false
  MakeFace = true
  OffsetFill = false
  OffsetIntersection = false
  OffsetJoinType = 0
  OffsetOpenResult = false
  PartialLoad = false
  Relative = false
  Support = -> [Connect005]
  _Version = 2
FEATURE [PartDesign::FeaturePython] BaseBend011  label="cap_outer_BaseBend"  # WARN: FeaturePython — macro-defined, semantics opaque (R4)
  BendSide = 1
  BendSketch = -> Binder016
  MidPlane = false
  Reverse = false
  Suppressed = false
  length = 67.6
  radius = 0.1
  thickness = 0.3
FEATURE [PartDesign::FeaturePython] Extend002  # WARN: FeaturePython — macro-defined, semantics opaque (R4)
  BaseFeature = -> BaseBend011
  Offset = 0.02
  Refine = true
  Suppressed = false
  UseSubtraction = false
  baseObject = -> BaseBend011 [Face1]
  gap1 = 0
  gap2 = 0
  length = 0
FEATURE [PartDesign::FeaturePython] Bend003  # WARN: FeaturePython — macro-defined, semantics opaque (R4)
  AutoMiter = true
  BaseFeature = -> Extend002
  BendType = 0
  LengthList = [20]
  LengthSpec = 1
  ReliefFactor = 0.7
  Suppressed = false
  UseReliefFactor = false
  angle = 90
  baseObject = -> Extend002 [Edge4,Edge17,Edge75,Edge46,Edge63]
  bendAList = [90]
  extend1 = 0
  extend2 = 0
  gap1 = 0
  gap2 = 0
  invert = false
  kfactor = 0.5
  length = 20
  maxExtendDist = 5
  minGap = 0.0353553
  minReliefGap = 0.2
  miterangle1 = 0
  miterangle2 = 0
  offset = 0
  radius = 0.1
  reliefType = 0
  reliefd = 1
  reliefw = 0.8
  sketchflip = false
  sketchinvert = false
  unfold = false
  expr: minGap = 0.05 mm / sqrt(2)
  expr: radius = BaseBend011.radius
FEATURE [PartDesign::Boolean] Boolean011
  BaseFeature = -> Bend003
  Group = -> [Body011]
  Refine = true
  Suppressed = false
  Type = 0
  UsePlacement = true
FEATURE [PartDesign::CoordinateSystem] Local_CS017  label="cap_outer_LCS"
  AttacherType = Attacher::AttachEngine3D
  AttachmentSupport = -> [XY_Plane011]
  MapMode = 5
FEATURE [PartDesign::Boolean] Boolean012
  BaseFeature = -> Boolean011
  Group = -> [Fusion013]
  Suppressed = false
  Type = 1
  UsePlacement = true
FEATURE [PartDesign::Body] Body010  label="cap_outer"
  Group = -> [Binder016,BaseBend011,Extend002,Bend003,Boolean011,Boolean012,Local_CS017]
  Origin = -> Origin011
  Tip = -> Boolean012
COMPONENT P7 — recipe-attached ("Body", modeled in this document).
Construction recipe (the document's own serialized feature program — sketch geometry with constraints, then the solid features built on it; lengths are millimeters unless a unit is written):

FEATURE [PartDesign::SubShapeBinder] Binder017
  BindCopyOnChange = 0
  BindMode = 0
  ClaimChildren = true
  Context = -> Body011 [Binder017.]
  Fuse = false
  MakeFace = true
  OffsetFill = false
  OffsetIntersection = false
  OffsetJoinType = 0
  OffsetOpenResult = false
  PartialLoad = false
  Placement = pos=(0,0,0) rot=(0.57735,0.57735,0.57735;2.0944rad)
  Relative = false
  Support = -> [Sketch058]
  _Version = 2
  expr: Placement = <<Sketch060>>.Placement
FEATURE [PartDesign::FeaturePython] BaseBend012  # WARN: FeaturePython — macro-defined, semantics opaque (R4)
  BendSide = 0
  BendSketch = -> Binder017
  MidPlane = true
  Reverse = false
  Suppressed = false
  length = 854.173
  radius = 0.1
  thickness = 0.3
  expr: length = <<Sketch059>>.Constraints.back_length - 0.1 mm
FEATURE [PartDesign::Body] Body011  label="Body"
  Group = -> [Binder017,BaseBend012]
  Origin = -> Origin012
  Tip = -> BaseBend012
COMPONENT P8 — recipe-attached ("cap_inner", modeled in this document).
Construction recipe (the document's own serialized feature program — sketch geometry with constraints, then the solid features built on it; lengths are millimeters unless a unit is written):

FEATURE [PartDesign::SubShapeBinder] Binder018
  BindCopyOnChange = 0
  BindMode = 0
  ClaimChildren = true
  Context = -> Body012 [Binder018.]
  Fuse = false
  MakeFace = true
  OffsetFill = false
  OffsetIntersection = false
  OffsetJoinType = 0
  OffsetOpenResult = false
  PartialLoad = false
  Placement = pos=(0,0,64.7) rot=(0,0,1;0rad)
  Relative = false
  Support = -> [Sketch059]
  _Version = 2
  expr: .Placement.Base.z = <<cap_outer_BaseBend>>.length + 0.1 mm - 3 mm
FEATURE [PartDesign::FeaturePython] BaseBend013  # WARN: FeaturePython — macro-defined, semantics opaque (R4)
  BendSide = 0
  BendSketch = -> Binder018
  MidPlane = false
  Reverse = false
  Suppressed = false
  length = 100
  radius = 0.1
  thickness = 0.3
FEATURE [PartDesign::FeaturePython] Bend004  # WARN: FeaturePython — macro-defined, semantics opaque (R4)
  AutoMiter = false
  BaseFeature = -> BaseBend013
  BendType = 1
  LengthList = [64.6]
  LengthSpec = 0
  ReliefFactor = 0.7
  Suppressed = false
  UseReliefFactor = false
  angle = 90
  baseObject = -> BaseBend013 [Edge3,Edge6]
  bendAList = [90]
  extend1 = 0
  extend2 = 0
  gap1 = 0
  gap2 = 3
  invert = false
  kfactor = 0.5
  length = 64.6
  maxExtendDist = 5
  minGap = 0.2
  minReliefGap = 1
  miterangle1 = 0
  miterangle2 = 0
  offset = 0
  radius = 0.1
  reliefType = 0
  reliefd = 1
  reliefw = 0.8
  sketchflip = false
  sketchinvert = false
  unfold = false
  expr: length = <<Binder018>>.Placement.Base.z - 0.1 mm
  expr: radius = BaseBend013.radius
FEATURE [PartDesign::CoordinateSystem] Local_CS018  label="cap_inner_LCS"
  AttacherType = Attacher::AttachEngine3D
  AttachmentSupport = -> [XY_Plane013]
  MapMode = 5
FEATURE [Sketcher::SketchObject] Sketch084
  AttachmentOffset = pos=(0,0,444.137) rot=(0,0,1;0rad)
  AttachmentSupport = -> [YZ_Plane013]
  FullyConstrained = true
  MapMode = 5
  Placement = pos=(444.137,0,0) rot=(0.57735,0.57735,0.57735;2.0944rad)
  expr: .AttachmentOffset.Base.z = <<cap_inner_base_Sketch>>.Constraints.offset
  expr: Constraints[17] = <<cap_fix_placement>>.Placement.Base.y
  expr: Constraints[18] = <<cap_fix_Sketch>>.Constraints.length - 3.2 mm / 2
  sketch-geometry (7):
    g0: LineSegment StartX=59.2 StartY=0 StartZ=0 EndX=40.8 EndY=0 EndZ=0
    g1: LineSegment StartX=40.8 StartY=0 StartZ=0 EndX=40.8 EndY=-3 EndZ=0
    g2: LineSegment StartX=40.8 StartY=-3 StartZ=0 EndX=43.8 EndY=-6 EndZ=0
    g3: LineSegment StartX=43.8 StartY=-6 StartZ=0 EndX=56.2 EndY=-6 EndZ=0
    g4: LineSegment StartX=56.2 StartY=-6 StartZ=0 EndX=59.2 EndY=-3 EndZ=0
    g5: LineSegment StartX=59.2 StartY=-3 StartZ=0 EndX=59.2 EndY=0 EndZ=0
    g6: GeomPoint X=50 Y=0 Z=0
  constraints (19):
    c: PointOnObject(g0,g-1)
    c: Coincident(g0,g1)
    c: Vertical(g1)
    c: Coincident(g1,g2)
    c: Coincident(g2,g3)
    c: Coincident(g3,g4)
    c: Coincident(g4,g5)
    c: Coincident(g5,g0)
    c: Vertical(g5)
    c: Equal(g5,g1)
    c: Equal(g4,g2)
    c: Horizontal(g3)
    c: DistanceY(g1,g0) = 3
    c: DistanceY(g2,g1) = 3
    c: Angle(g2) = -0.785398
    c: Symmetric(g0,g0,g6)
    c: Horizontal(g0)
    c: DistanceX(g6) = 50
    c: DistanceX(g0,g0) = 18.4
FEATURE [PartDesign::Pad] Pad026
  BaseFeature = -> Bend004
  Direction = (1,0,0)
  Length = 0.3
  Length2 = 10
  Profile = -> Sketch084
  ReferenceAxis = -> Sketch084 [N_Axis]
  Refine = true
  Reversed = true
  Suppressed = false
  Type = 0
FEATURE [PartDesign::Boolean] Boolean013
  BaseFeature = -> Pad026
  Group = -> [Fusion014]
  Suppressed = false
  Type = 1
  UsePlacement = true
FEATURE [PartDesign::Body] Body012  label="cap_inner"
  Group = -> [Binder018,BaseBend013,Bend004,Pad026,Boolean013,Local_CS018,Sketch084]
  Origin = -> Origin013
  Tip = -> Pad026
COMPONENT P9 — recipe-attached ("basin_fix", modeled in this document).
Construction recipe (the document's own serialized feature program — sketch geometry with constraints, then the solid features built on it; lengths are millimeters unless a unit is written):

FEATURE [PartDesign::SubShapeBinder] Binder022
  BindCopyOnChange = 0
  BindMode = 0
  ClaimChildren = true
  Context = -> Body015 [Binder022.]
  Fuse = false
  MakeFace = true
  OffsetFill = false
  OffsetIntersection = false
  OffsetJoinType = 0
  OffsetOpenResult = false
  PartialLoad = false
  Relative = false
  Support = -> [Connect006]
  _Version = 2
FEATURE [PartDesign::SubShapeBinder] Binder023
  BindCopyOnChange = 0
  BindMode = 0
  ClaimChildren = true
  Context = -> Body015 [Binder023.]
  Fuse = false
  MakeFace = true
  OffsetFill = false
  OffsetIntersection = false
  OffsetJoinType = 0
  OffsetOpenResult = false
  PartialLoad = false
  Relative = true
  Support = -> [Sketch069]
  _Version = 2
FEATURE [PartDesign::Pad] Pad014
  Direction = (0,0,1)
  Length = 3
  Length2 = 10
  Profile = -> Binder022
  Suppressed = false
  Type = 0
FEATURE [PartDesign::Pocket] Pocket008
  BaseFeature = -> Pad014
  Direction = (0,0,-1)
  Length = 5
  Length2 = 5
  Profile = -> Binder023
  Reversed = true
  Suppressed = false
  Type = 0
FEATURE [PartDesign::CoordinateSystem] Local_CS024  label="basin_fix_LCS"
  AttacherType = Attacher::AttachEngine3D
  AttachmentOffset = pos=(0,0,-3) rot=(0,0,1;0rad)
  AttachmentSupport = -> [XY_Plane016]
  MapMode = 5
  Placement = pos=(0,0,-3) rot=(0,0,1;0rad)
FEATURE [PartDesign::Body] Body015  label="basin_fix"
  Group = -> [Binder022,Binder023,Pad014,Pocket008,Local_CS024]
  Origin = -> Origin016
  Tip = -> Pocket008
COMPONENT P10 — recipe-attached ("door_plexiglass", modeled in this document).
Construction recipe (the document's own serialized feature program — sketch geometry with constraints, then the solid features built on it; lengths are millimeters unless a unit is written):

FEATURE [PartDesign::SubShapeBinder] Binder024
  BindCopyOnChange = 0
  BindMode = 0
  ClaimChildren = true
  Context = -> Body016 [Binder024.]
  Fuse = false
  MakeFace = true
  OffsetFill = false
  OffsetIntersection = false
  OffsetJoinType = 0
  OffsetOpenResult = false
  PartialLoad = false
  Relative = true
  Support = -> [Sketch070]
  _Version = 2
FEATURE [PartDesign::FeaturePython] BaseBend015  label="door_plexiglass_BaseBend"  # WARN: FeaturePython — macro-defined, semantics opaque (R4)
  BendSide = 0
  BendSketch = -> Binder024
  MidPlane = false
  Reverse = false
  Suppressed = false
  length = 911
  radius = 1
  thickness = 4
FEATURE [PartDesign::CoordinateSystem] Local_CS025
  AttacherType = Attacher::AttachEngine3D
  AttachmentOffset = pos=(447.137,0,0) rot=(0,0,1;0rad)
  AttachmentSupport = -> [XY_Plane017]
  MapMode = 5
  Placement = pos=(447.137,0,0) rot=(0,0,1;0rad)
  expr: .AttachmentOffset.Base.x = <<door_plexiglass_Sketch>>.Constraints.length
FEATURE [PartDesign::Boolean] Boolean015
  BaseFeature = -> BaseBend015
  Group = -> [Fusion016]
  Suppressed = false
  Type = 1
  UsePlacement = true
FEATURE [PartDesign::Body] Body016  label="door_plexiglass"
  Group = -> [Binder024,BaseBend015,Boolean015,Local_CS025]
  Origin = -> Origin017
  Tip = -> Boolean015
COMPONENT P11 — recipe-attached ("sink_cutout", modeled in this document).
Construction recipe (the document's own serialized feature program — sketch geometry with constraints, then the solid features built on it; lengths are millimeters unless a unit is written):

FEATURE [PartDesign::SubShapeBinder] Binder029
  BindCopyOnChange = 0
  BindMode = 0
  ClaimChildren = true
  Context = -> Body018 [Binder029.]
  Fuse = false
  MakeFace = true
  OffsetFill = false
  OffsetIntersection = false
  OffsetJoinType = 0
  OffsetOpenResult = false
  PartialLoad = false
  Relative = true
  Support = -> [Offset2D]
  _Version = 2
FEATURE [PartDesign::Pad] Pad027
  Direction = (0,0,1)
  Length = 1.5
  Length2 = 10
  Profile = -> Binder029
  Suppressed = false
  Type = 0
FEATURE [PartDesign::CoordinateSystem] Local_CS028  label="sink_cutout_LCS"
  AttacherType = Attacher::AttachEngine3D
  AttachmentSupport = -> [XY_Plane019]
  MapMode = 5
FEATURE [Sketcher::SketchObject] Sketch115
  FullyConstrained = true
  sketch-geometry (1):
    g0: Circle CenterX=0 CenterY=50 CenterZ=0 NormalX=0 NormalY=0 NormalZ=1 AngleXU=0 Radius=15
  constraints (3):
    c: PointOnObject(g0,g-2)
    c: Diameter(g0) = 30
    c: DistanceY(g0) = 50
FEATURE [PartDesign::Pocket] Pocket017
  BaseFeature = -> Pad027
  Direction = (0,0,-1)
  Length = 5
  Length2 = 5
  Midplane = true
  Profile = -> Sketch115
  ReferenceAxis = -> Sketch115 [N_Axis]
  Suppressed = false
  Type = 0
FEATURE [PartDesign::Body] Body018  label="sink_cutout"
  Group = -> [Binder029,Pad027,Local_CS028,Sketch115,Pocket017]
  Origin = -> Origin019
  Tip = -> Pocket017
COMPONENT P12 — recipe-attached ("sink_jumb", modeled in this document).
Construction recipe (the document's own serialized feature program — sketch geometry with constraints, then the solid features built on it; lengths are millimeters unless a unit is written):

FEATURE [PartDesign::SubShapeBinder] Binder030
  BindCopyOnChange = 0
  BindMode = 0
  ClaimChildren = true
  Context = -> Body019 [Binder030.]
  Fuse = false
  MakeFace = true
  OffsetFill = false
  OffsetIntersection = false
  OffsetJoinType = 0
  OffsetOpenResult = false
  PartialLoad = false
  Relative = false
  Support = -> [Sketch087]
  _Version = 2
FEATURE [PartDesign::Pad] Pad028
  Direction = (0,0,1)
  Length = 0.7
  Length2 = 10
  Profile = -> Binder030
  Suppressed = false
  Type = 0
FEATURE [PartDesign::Boolean] Boolean016
  BaseFeature = -> Pad028
  Group = -> [Fusion017]
  Suppressed = false
  Type = 1
  UsePlacement = true
FEATURE [PartDesign::CoordinateSystem] Local_CS030  label="sink_jumb_LCS"
  AttacherType = Attacher::AttachEngine3D
  AttachmentOffset = pos=(0,0,0.7) rot=(0,0,1;0rad)
  AttachmentSupport = -> [XY_Plane020]
  MapMode = 5
  Placement = pos=(0,0,0.7) rot=(0,0,1;0rad)
FEATURE [PartDesign::Body] Body019  label="sink_jumb"
  Group = -> [Binder030,Pad028,Boolean016,Local_CS030]
  Origin = -> Origin020
  Tip = -> Boolean016
COMPONENT P13 — recipe-attached ("Body020", modeled in this document).
Construction recipe (the document's own serialized feature program — sketch geometry with constraints, then the solid features built on it; lengths are millimeters unless a unit is written):

FEATURE [Sketcher::SketchObject] Sketch088
  AttachmentSupport = -> [XY_Plane021]
  FullyConstrained = true
  MapMode = 5
  expr: Constraints[11] = <<Dimensions>>.Constraints.width
  sketch-geometry (5):
    g0: LineSegment StartX=-447.137 StartY=0 StartZ=0 EndX=447.137 EndY=0 EndZ=0
    g1: LineSegment StartX=447.137 StartY=0 StartZ=0 EndX=447.137 EndY=270 EndZ=0
    g2: LineSegment StartX=447.137 StartY=270 StartZ=0 EndX=-447.137 EndY=270 EndZ=0
    g3: LineSegment StartX=-447.137 StartY=270 StartZ=0 EndX=-447.137 EndY=0 EndZ=0
    g4: GeomPoint X=0 Y=135 Z=0
  constraints (13):
    c: Coincident(g0,g1)
    c: Coincident(g1,g2)
    c: Coincident(g2,g3)
    c: Coincident(g3,g0)
    c: Horizontal(g0)
    c: Horizontal(g2)
    c: Vertical(g1)
    c: Vertical(g3)
    c: Symmetric(g2,g0,g4)
    c: PointOnObject(g4,g-2)
    c: PointOnObject(g0,g-1)
    c: DistanceX(g0,g1) = 894.273
    c: DistanceY(g0,g1) = 270
FEATURE [PartDesign::Pad] Pad029
  Direction = (0,0,1)
  Length = 300
  Length2 = 10
  Profile = -> Sketch088
  ReferenceAxis = -> Sketch088 [N_Axis]
  Suppressed = false
  Type = 0
FEATURE [PartDesign::Body] Body020
  Group = -> [Sketch088,Pad029]
  Origin = -> Origin021
  Tip = -> Pad029
COMPONENT P14 — recipe-attached ("Body021", modeled in this document).
Construction recipe (the document's own serialized feature program — sketch geometry with constraints, then the solid features built on it; lengths are millimeters unless a unit is written):

FEATURE [PartDesign::SubShapeBinder] Binder032
  BindCopyOnChange = 0
  BindMode = 0
  ClaimChildren = true
  Context = -> Body021 [Binder032.]
  Fuse = false
  MakeFace = true
  OffsetFill = false
  OffsetIntersection = false
  OffsetJoinType = 0
  OffsetOpenResult = false
  PartialLoad = false
  Relative = false
  Support = -> [Connect008]
  _Version = 2
FEATURE [PartDesign::FeaturePython] BaseBend016  # WARN: FeaturePython — macro-defined, semantics opaque (R4)
  BendSide = 0
  BendSketch = -> Binder032
  MidPlane = true
  Reverse = false
  Suppressed = false
  length = 882.273
  radius = 0.1
  thickness = 0.3
  expr: length = <<bar_BaseBend>>.length - 6 mm
FEATURE [PartDesign::FeaturePython] Extend003  # WARN: FeaturePython — macro-defined, semantics opaque (R4)
  BaseFeature = -> BaseBend016
  Offset = 0.02
  Refine = true
  Suppressed = false
  UseSubtraction = false
  baseObject = -> BaseBend016 [Face1]
  gap1 = 0
  gap2 = 0
  length = 0
FEATURE [PartDesign::FeaturePython] Bend006  # WARN: FeaturePython — macro-defined, semantics opaque (R4)
  AutoMiter = true
  BaseFeature = -> Extend003
  BendType = 0
  LengthList = [30]
  LengthSpec = 0
  ReliefFactor = 0.7
  Suppressed = false
  UseReliefFactor = false
  angle = 90
  baseObject = -> Extend003 [Edge75,Edge39]
  bendAList = [90]
  extend1 = 0
  extend2 = 0
  gap1 = 0
  gap2 = 0
  invert = false
  kfactor = 0.5
  length = 30
  maxExtendDist = 5
  minGap = 0.2
  minReliefGap = 1
  miterangle1 = 0
  miterangle2 = 0
  offset = 0
  radius = 0.1
  reliefType = 0
  reliefd = 1
  reliefw = 0.8
  sketchflip = false
  sketchinvert = false
  unfold = false
  expr: radius = <<BaseBend016>>.radius
FEATURE [PartDesign::Boolean] Boolean017
  BaseFeature = -> Bend006
  Group = -> [Fusion018]
  Suppressed = false
  Type = 1
  UsePlacement = true
FEATURE [PartDesign::Body] Body021
  Group = -> [Binder032,BaseBend016,Extend003,Bend006,Boolean017]
  Origin = -> Origin022
  Tip = -> Boolean017
COMPONENT P15 — recipe-attached ("door_jumb", modeled in this document).
Construction recipe (the document's own serialized feature program — sketch geometry with constraints, then the solid features built on it; lengths are millimeters unless a unit is written):

FEATURE [PartDesign::SubShapeBinder] Binder033
  BindCopyOnChange = 0
  BindMode = 0
  ClaimChildren = true
  Context = -> Body022 [Binder033.]
  Fuse = false
  MakeFace = true
  OffsetFill = false
  OffsetIntersection = false
  OffsetJoinType = 0
  OffsetOpenResult = false
  PartialLoad = false
  Placement = pos=(0,0,0) rot=(0.57735,0.57735,0.57735;2.0944rad)
  Relative = false
  Support = -> [Sketch090]
  _Version = 2
  expr: Placement = Support[0][0].Placement
FEATURE [PartDesign::CoordinateSystem] Local_CS033  label="door_jumb_LCS"
  AttacherType = Attacher::AttachEngine3D
  AttachmentSupport = -> [XY_Plane023]
  MapMode = 5
FEATURE [PartDesign::FeaturePython] BaseBend017  # WARN: FeaturePython — macro-defined, semantics opaque (R4)
  BendSide = 1
  BendSketch = -> Binder033
  MidPlane = true
  Reverse = false
  Suppressed = false
  length = 100
  radius = 0.1
  thickness = 0.3
FEATURE [PartDesign::FeaturePython] Bend007  # WARN: FeaturePython — macro-defined, semantics opaque (R4)
  AutoMiter = true
  BaseFeature = -> BaseBend017
  BendType = 1
  LengthList = [3]
  LengthSpec = 1
  ReliefFactor = 0.7
  Suppressed = false
  UseReliefFactor = false
  angle = 90
  baseObject = -> BaseBend017 [Edge16,Edge17]
  bendAList = [90]
  extend1 = 0
  extend2 = 0
  gap1 = 0
  gap2 = 0
  invert = false
  kfactor = 0.5
  length = 3
  maxExtendDist = 5
  minGap = 0.2
  minReliefGap = 1
  miterangle1 = 0
  miterangle2 = 0
  offset = 0
  radius = 0.1
  reliefType = 0
  reliefd = 1
  reliefw = 0.8
  sketchflip = false
  sketchinvert = false
  unfold = false
  expr: radius = BaseBend017.radius
FEATURE [Sketcher::SketchObject] Sketch091
  AttachmentOffset = pos=(0,0,50) rot=(0,0,1;0rad)
  AttachmentSupport = -> [YZ_Plane023]
  ExternalGeometry = -> [Binder033]
  FullyConstrained = true
  MapMode = 5
  Placement = pos=(50,0,0) rot=(0.57735,0.57735,0.57735;2.0944rad)
  expr: .AttachmentOffset.Base.z = <<BaseBend017>>.length / 2
  sketch-geometry (3):
    g0: LineSegment StartX=0 StartY=3 StartZ=0 EndX=85.0634 EndY=46.3371 EndZ=0
    g1: LineSegment StartX=85.0634 StartY=46.3371 StartZ=0 EndX=85.0634 EndY=3 EndZ=0
    g2: LineSegment StartX=85.0634 StartY=3 StartZ=0 EndX=0 EndY=3 EndZ=0
  constraints (9):
    c: PointOnObject(g0,g-2)
    c: Coincident(g0,g1)
    c: Vertical(g1)
    c: Coincident(g1,g2)
    c: Coincident(g2,g0)
    c: Horizontal(g2)
    c: DistanceY(g0) = 3
    c: Horizontal(g-3,g0)
    c: DistanceX(g0,g-3) = 3.4
FEATURE [PartDesign::Pad] Pad030
  BaseFeature = -> Bend007
  Direction = (1,0,0)
  Length = 0.3
  Length2 = 10
  Profile = -> Sketch091
  ReferenceAxis = -> Sketch091 [N_Axis]
  Refine = true
  Reversed = true
  Suppressed = false
  Type = 0
FEATURE [PartDesign::SubShapeBinder] Binder034
  BindCopyOnChange = 0
  BindMode = 0
  ClaimChildren = true
  Context = -> Body022 [Binder034.]
  Fuse = false
  MakeFace = true
  OffsetFill = false
  OffsetIntersection = false
  OffsetJoinType = 0
  OffsetOpenResult = false
  PartialLoad = false
  Relative = false
  Support = -> [Part__Mirroring023]
  _Version = 2
FEATURE [PartDesign::Pad] Pad031
  BaseFeature = -> Pad030
  Direction = (1,0,0)
  Length = 0.3
  Length2 = 10
  Profile = -> Binder034
  Suppressed = false
  Type = 0
FEATURE [PartDesign::Boolean] Boolean018
  BaseFeature = -> Pad031
  Group = -> [Fusion019]
  Suppressed = false
  Type = 1
  UsePlacement = true
FEATURE [PartDesign::Body] Body022  label="door_jumb"
  Group = -> [Binder033,Local_CS033,BaseBend017,Bend007,Sketch091,Pad030,Binder034,Pad031,Boolean018]
  Origin = -> Origin023
  Tip = -> Boolean018
COMPONENT P16 — recipe-attached ("pan_face", modeled in this document).
Construction recipe (the document's own serialized feature program — sketch geometry with constraints, then the solid features built on it; lengths are millimeters unless a unit is written):

FEATURE [PartDesign::SubShapeBinder] Binder035
  BindCopyOnChange = 0
  BindMode = 0
  ClaimChildren = true
  Context = -> Body023 [Binder035.]
  Fuse = false
  MakeFace = true
  OffsetFill = false
  OffsetIntersection = false
  OffsetJoinType = 0
  OffsetOpenResult = false
  PartialLoad = false
  Relative = false
  Support = -> [Sketch092]
  _Version = 2
FEATURE [PartDesign::Pad] Pad032
  Direction = (0,0,1)
  Length = 5
  Length2 = 10
  Profile = -> Binder035
  Suppressed = false
  Type = 0
FEATURE [PartDesign::CoordinateSystem] Local_CS036  label="pan_face_LCS"
  AttacherType = Attacher::AttachEngine3D
  AttachmentSupport = -> [XY_Plane024]
  MapMode = 5
FEATURE [PartDesign::Boolean] Boolean019
  BaseFeature = -> Pad032
  Group = -> [Fusion020]
  Suppressed = false
  Type = 1
  UsePlacement = true
FEATURE [PartDesign::Body] Body023  label="pan_face"
  Group = -> [Binder035,Pad032,Local_CS036,Boolean019]
  Origin = -> Origin024
  Tip = -> Boolean019
COMPONENT P17 — recipe-attached ("bottom_amplifier", modeled in this document).
Construction recipe (the document's own serialized feature program — sketch geometry with constraints, then the solid features built on it; lengths are millimeters unless a unit is written):

FEATURE [PartDesign::SubShapeBinder] Binder036
  BindCopyOnChange = 0
  BindMode = 0
  ClaimChildren = true
  Context = -> Body024 [Binder036.]
  Fuse = false
  MakeFace = true
  OffsetFill = false
  OffsetIntersection = false
  OffsetJoinType = 0
  OffsetOpenResult = false
  PartialLoad = false
  Placement = pos=(0,0,0) rot=(0.57735,0.57735,0.57735;2.0944rad)
  Relative = false
  Support = -> [Sketch095]
  _Version = 2
  expr: Placement = Support[0][0].Placement
FEATURE [PartDesign::FeaturePython] BaseBend018  # WARN: FeaturePython — macro-defined, semantics opaque (R4)
  BendSide = 1
  BendSketch = -> Binder036
  MidPlane = false
  Reverse = true
  Suppressed = false
  length = 150
  radius = 0.1
  thickness = 0.3
FEATURE [PartDesign::FeaturePython] Bend008  # WARN: FeaturePython — macro-defined, semantics opaque (R4)
  AutoMiter = false
  BaseFeature = -> BaseBend018
  BendType = 1
  LengthList = [0.5]
  LengthSpec = 1
  ReliefFactor = 0.7
  Suppressed = false
  UseReliefFactor = false
  angle = 90
  baseObject = -> BaseBend018 [Edge17,Edge33,Edge49]
  bendAList = [90]
  extend1 = 0
  extend2 = 0
  gap1 = 1
  gap2 = 1
  invert = false
  kfactor = 0.5
  length = 0.5
  maxExtendDist = 5
  minGap = 0.2
  minReliefGap = 1
  miterangle1 = 0
  miterangle2 = 0
  offset = 0
  radius = 0.1
  reliefType = 0
  reliefd = 1
  reliefw = 0.8
  sketchflip = false
  sketchinvert = false
  unfold = false
  expr: miterangle1 = 0
  expr: miterangle2 = miterangle1
  expr: radius = BaseBend018.radius
FEATURE [PartDesign::CoordinateSystem] Local_CS037  label="bottom_amplifier_LCS"
  AttacherType = Attacher::AttachEngine3D
  AttachmentSupport = -> [XY_Plane025]
  MapMode = 5
FEATURE [Sketcher::SketchObject] Sketch096
  AttachmentSupport = -> [YZ_Plane025]
  ExternalGeometry = -> [Binder036]
  FullyConstrained = true
  MapMode = 5
  Placement = pos=(0,0,0) rot=(0.57735,0.57735,0.57735;2.0944rad)
  sketch-geometry (30):
    g0: LineSegment StartX=23.2071 StartY=45.5 StartZ=0 EndX=37.7071 EndY=60 EndZ=0
    g1: LineSegment StartX=37.7071 StartY=60 StartZ=0 EndX=164.499 EndY=60 EndZ=0
    g2: LineSegment StartX=164.499 StartY=60 StartZ=0 EndX=195.949 EndY=45.5 EndZ=0
    g3: LineSegment StartX=195.949 StartY=45.5 StartZ=0 EndX=23.2071 EndY=45.5 EndZ=0
    g4: LineSegment StartX=22.5 StartY=46.2071 StartZ=0 EndX=37 EndY=60.7071 EndZ=0
    g5: LineSegment StartX=37 StartY=60.7071 StartZ=0 EndX=37 EndY=214.964 EndZ=0
    g6: LineSegment StartX=22.5 StartY=241 StartZ=0 EndX=22.5 EndY=46.2071 EndZ=0
    g7: LineSegment StartX=196.367 StartY=46.4081 StartZ=0 EndX=164.918 EndY=60.9081 EndZ=0
    g8: LineSegment StartX=164.918 StartY=60.9081 StartZ=0 EndX=42.8123 EndY=203.898 EndZ=0
    g9: LineSegment StartX=42.8123 StartY=203.898 StartZ=0 EndX=27.8325 EndY=238.981 EndZ=0
    g10: LineSegment StartX=30 StartY=242 StartZ=0 EndX=26 EndY=242 EndZ=0
    g11: LineSegment StartX=26 StartY=242 StartZ=0 EndX=22 EndY=242 EndZ=0
    g12: LineSegment StartX=22 StartY=45 StartZ=0 EndX=110.114 EndY=45 EndZ=0
    g13: LineSegment StartX=110.114 StartY=45 StartZ=0 EndX=198.227 EndY=45 EndZ=0
    g14: LineSegment StartX=26 StartY=242 StartZ=0 EndX=110.114 EndY=45 EndZ=0
    g15: LineSegment StartX=22 StartY=45 StartZ=0 EndX=22 EndY=126.25 EndZ=0
    g16: LineSegment StartX=22 StartY=126.25 StartZ=0 EndX=83.7873 EndY=179.013 EndZ=0
    g17: LineSegment StartX=22 StartY=126.25 StartZ=0 EndX=198.227 EndY=45 EndZ=0
    g18: LineSegment StartX=22 StartY=45 StartZ=0 EndX=117.055 EndY=140.055 EndZ=0
    g19: LineSegment StartX=27.8325 StartY=238.981 StartZ=0 EndX=30.1964 EndY=241 EndZ=0
    g20: LineSegment StartX=30.1964 StartY=241 StartZ=0 EndX=196.367 EndY=46.4081 EndZ=0
    g21: LineSegment StartX=37 StartY=214.964 StartZ=0 EndX=25.8833 EndY=241 EndZ=0
    g22: LineSegment StartX=25.8833 StartY=241 StartZ=0 EndX=22.5 EndY=241 EndZ=0
    g23: LineSegment StartX=37 StartY=214.964 StartZ=0 EndX=37.4598 EndY=215.16 EndZ=0
    g24: LineSegment StartX=37.4598 StartY=215.16 StartZ=0 EndX=37.9197 EndY=215.357 EndZ=0
    g25: LineSegment StartX=37 StartY=60.7071 StartZ=0 EndX=37.3536 EndY=60.3536 EndZ=0
    g26: LineSegment StartX=164.499 StartY=60 StartZ=0 EndX=164.708 EndY=60.4541 EndZ=0
    g27: LineSegment StartX=37.7071 StartY=60 StartZ=0 EndX=37.7071 EndY=45 EndZ=0
    g28: LineSegment StartX=37 StartY=60.7071 StartZ=0 EndX=22 EndY=60.7071 EndZ=0
    g29: LineSegment StartX=164.918 StartY=60.9081 StartZ=0 EndX=176.324 EndY=70.649 EndZ=0
  constraints (85):
    c: Coincident(g0,g1)
    c: Horizontal(g1)
    c: Coincident(g1,g2)
    c: Coincident(g2,g3)
    c: Coincident(g3,g0)
    c: Horizontal(g3)
    c: Coincident(g4,g5)
    c: Vertical(g5)
    c: Coincident(g5,g21)
    c: Coincident(g22,g6)
    c: Coincident(g6,g4)
    c: Vertical(g6)
    c: Coincident(g20,g7)
    c: Coincident(g7,g8)
    c: Coincident(g8,g9)
    c: Coincident(g9,g19)
    c: Coincident(g-3,g10)
    c: Horizontal(g10)
    c: Coincident(g10,g11)
    c: PointOnObject(g11,g-4)
    c: Horizontal(g11)
    c: Coincident(g12,g13)
    c: Symmetric(g12,g13,g12)
    c: Coincident(g13,g-3)
    c: Coincident(g12,g-4)
    c: Coincident(g14,g10)
    c: Coincident(g14,g12)
    c: Vertical(g15)
    c: Coincident(g15,g16)
    c: PointOnObject(g16,g-3)
    c: PointOnObject(g15,g12)
    c: Perpendicular(g-3,g16)
    c: Equal(g15,g16)
    c: PointOnObject(g15,g-4)
    c: Coincident(g17,g15)
    c: Coincident(g17,g13)
    c: Parallel(g2,g17)
    c: Parallel(g17,g7)
    c: Coincident(g18,g15)
    c: PointOnObject(g18,g-3)
    c: Angle(g18) = 0.785398
    c: Parallel(g0,g18)
    c: Parallel(g18,g4)
    c: Parallel(g14,g9)
    c: DistanceY(g12,g0) = 0.5
    c: DistanceX(g12,g4) = 0.5
    c: Distance(g20,g-3) = 0.5
    c: Symmetric(g1,g7,g17)
    c: Symmetric(g0,g4,g18)
    c: Coincident(g19,g20)
    c: Parallel(g-3,g20)
    c: Perpendicular(g20,g19)
    c: Coincident(g21,g22)
    c: Parallel(g21,g14)
    c: Horizontal(g22)
    c: Equal(g11,g10)
    c: Coincident(g5,g23)
    c: PointOnObject(g23,g14)
    c: Coincident(g23,g24)
    c: PointOnObject(g24,g9)
    c: Coincident(g4,g25)
    c: PointOnObject(g25,g18)
    c: Coincident(g1,g26)
    c: PointOnObject(g26,g17)
    c: Perpendicular(g17,g26)
    c: Perpendicular(g18,g25)
    c: Perpendicular(g14,g23)
    c: Equal(g24,g23)
    c: Equal(g23,g25)
    c: Equal(g25,g26)
    c: Parallel(g24,g23)
    c: Distance(g5,g24) = 1
    c: Distance(g19,g10) = 1
    c: DistanceY(g6,g11) = 1
    c: Coincident(g27,g0)
    c: PointOnObject(g27,g12)
    c: Vertical(g27)
    c: Coincident(g28,g4)
    c: PointOnObject(g28,g15)
    c: Horizontal(g28)
    c: Coincident(g29,g7)
    c: PointOnObject(g29,g-3)
    c: Perpendicular(g-3,g29)
    c: Distance(g29) = 15  'length'
    c: Parallel(g8,g20)
FEATURE [PartDesign::Pad] Pad033
  BaseFeature = -> Bend008
  Direction = (1,0,0)
  Length = 0.3
  Length2 = 10
  Profile = -> Sketch096
  ReferenceAxis = -> Sketch096 [N_Axis]
  Reversed = true
  Suppressed = false
  Type = 0
FEATURE [PartDesign::Boolean] Boolean020
  BaseFeature = -> Pad033
  Group = -> [Compound011]
  Suppressed = false
  Type = 1
  UsePlacement = true
FEATURE [PartDesign::Body] Body024  label="bottom_amplifier"
  Group = -> [Binder036,BaseBend018,Bend008,Local_CS037,Sketch096,Pad033,Boolean020]
  Origin = -> Origin025
  Tip = -> Boolean020
COMPONENT P18 — recipe-attached ("bottom", modeled in this document).
Construction recipe (the document's own serialized feature program — sketch geometry with constraints, then the solid features built on it; lengths are millimeters unless a unit is written):

FEATURE [PartDesign::SubShapeBinder] Binder037
  BindCopyOnChange = 0
  BindMode = 0
  ClaimChildren = true
  Context = -> Body025 [Binder037.]
  Fuse = false
  MakeFace = true
  OffsetFill = false
  OffsetIntersection = false
  OffsetJoinType = 0
  OffsetOpenResult = false
  PartialLoad = false
  Placement = pos=(0,0,0) rot=(1,0,0;1.5708rad)
  Relative = false
  Support = -> [Sketch098]
  _Version = 2
  expr: Placement = Support[0][0].Placement
FEATURE [PartDesign::FeaturePython] BaseBend019  # WARN: FeaturePython — macro-defined, semantics opaque (R4)
  BendSide = 1
  BendSketch = -> Binder037
  MidPlane = false
  Reverse = true
  Suppressed = false
  length = 250
  radius = 0.1
  thickness = 0.3
  expr: length = <<Dimensions>>.Constraints.depth - 15 mm
FEATURE [PartDesign::FeaturePython] Bend009  # WARN: FeaturePython — macro-defined, semantics opaque (R4)
  AutoMiter = true
  BaseFeature = -> BaseBend019
  BendType = 1
  LengthList = [40]
  LengthSpec = 1
  ReliefFactor = 0.7
  Suppressed = false
  UseReliefFactor = false
  angle = 90
  baseObject = -> BaseBend019 [Edge17]
  bendAList = [90]
  extend1 = 0
  extend2 = 0
  gap1 = 3
  gap2 = 3
  invert = false
  kfactor = 0.5
  length = 40
  maxExtendDist = 5
  minGap = 0.2
  minReliefGap = 1
  miterangle1 = 0
  miterangle2 = 0
  offset = 0
  radius = 0.1
  reliefType = 0
  reliefd = 1
  reliefw = 0.8
  sketchflip = false
  sketchinvert = false
  unfold = false
  expr: radius = BaseBend019.radius
FEATURE [PartDesign::CoordinateSystem] Local_CS039  label="bottom_bottom_front_connect_LCS"
  AttacherType = Attacher::AttachEngine3D
  AttachmentOffset = pos=(441.137,3,3) rot=(0,0,1;0rad)
  AttachmentSupport = -> [XY_Plane026]
  MapMode = 5
  Placement = pos=(441.137,3,3) rot=(0,0,1;0rad)
  expr: AttachmentOffset = <<bottom_front_connect_placement>>.Placement
FEATURE [PartDesign::CoordinateSystem] Local_CS040  label="bottom_LCS"
  AttacherType = Attacher::AttachEngine3D
  AttachmentSupport = -> [XY_Plane026]
  MapMode = 5
FEATURE [PartDesign::Boolean] Boolean022
  BaseFeature = -> Bend009
  Group = -> [Fusion022]
  Suppressed = false
  Type = 1
  UsePlacement = true
FEATURE [PartDesign::Body] Body025  label="bottom"
  Group = -> [Binder037,BaseBend019,Bend009,Boolean022,Local_CS039,Local_CS040]
  Origin = -> Origin026
  Tip = -> Boolean022
COMPONENT P19 — recipe-attached ("bottom_front_connect", modeled in this document).
Construction recipe (the document's own serialized feature program — sketch geometry with constraints, then the solid features built on it; lengths are millimeters unless a unit is written):

FEATURE [PartDesign::SubShapeBinder] Binder038
  BindCopyOnChange = 0
  BindMode = 0
  ClaimChildren = true
  Context = -> Body026 [Binder038.]
  Fuse = false
  MakeFace = true
  OffsetFill = false
  OffsetIntersection = false
  OffsetJoinType = 0
  OffsetOpenResult = false
  PartialLoad = false
  Relative = false
  Support = -> [Sketch099]
  _Version = 2
FEATURE [PartDesign::FeaturePython] BaseBend020  # WARN: FeaturePython — macro-defined, semantics opaque (R4)
  BendSide = 1
  BendSketch = -> Binder038
  MidPlane = false
  Reverse = false
  Suppressed = false
  length = 100
  radius = 0.1
  thickness = 0.3
FEATURE [Sketcher::SketchObject] Sketch100
  AttachmentSupport = -> [XZ_Plane027]
  FullyConstrained = true
  MapMode = 5
  Placement = pos=(0,0,0) rot=(1,0,0;1.5708rad)
  sketch-geometry (4):
    g0: LineSegment StartX=0 StartY=0 StartZ=0 EndX=0 EndY=39 EndZ=0
    g1: LineSegment StartX=0 StartY=39 StartZ=0 EndX=-20 EndY=39 EndZ=0
    g2: LineSegment StartX=-20 StartY=39 StartZ=0 EndX=-20 EndY=0 EndZ=0
    g3: LineSegment StartX=-20 StartY=0 StartZ=0 EndX=0 EndY=0 EndZ=0
  constraints (11):
    c: Coincident(g0,g1)
    c: Coincident(g1,g2)
    c: Coincident(g2,g3)
    c: Coincident(g3,g0)
    c: Vertical(g0)
    c: Vertical(g2)
    c: Horizontal(g1)
    c: Horizontal(g3)
    c: Coincident(g0,g-1)
    c: DistanceX(g0,g1) = -20
    c: DistanceY(g0,g1) = 39  'height'
FEATURE [PartDesign::CoordinateSystem] Local_CS041  label="bottom_front_connect_LCS"
  AttacherType = Attacher::AttachEngine3D
  AttachmentSupport = -> [XY_Plane027]
  MapMode = 5
FEATURE [Sketcher::SketchObject] Sketch101
  AttachmentSupport = -> [XZ_Plane027]
  FullyConstrained = true
  MapMode = 5
  Placement = pos=(0,0,0) rot=(1,0,0;1.5708rad)
  expr: Constraints[12] = <<BaseBend020>>.length
  sketch-geometry (5):
    g0: LineSegment StartX=-0.5 StartY=0 StartZ=0 EndX=-100.5 EndY=0 EndZ=0
    g1: LineSegment StartX=-100.5 StartY=0 StartZ=0 EndX=-100.5 EndY=40 EndZ=0
    g2: LineSegment StartX=-100.5 StartY=40 StartZ=0 EndX=-3 EndY=100 EndZ=0
    g3: LineSegment StartX=-3 StartY=100 StartZ=0 EndX=-0.5 EndY=100 EndZ=0
    g4: LineSegment StartX=-0.5 StartY=100 StartZ=0 EndX=-0.5 EndY=0 EndZ=0
  constraints (15):
    c: Horizontal(g0)
    c: Coincident(g0,g1)
    c: Vertical(g1)
    c: Coincident(g1,g2)
    c: Coincident(g2,g3)
    c: Coincident(g3,g4)
    c: Vertical(g4)
    c: Coincident(g0,g4)
    c: PointOnObject(g0,g-1)
    c: DistanceX(g0) = -0.5
    c: Horizontal(g3)
    c: DistanceX(g2) = -3
    c: DistanceY(g3) = 100
    c: DistanceX(g0,g0) = 100
    c: DistanceY(g1,g1) = 40
FEATURE [PartDesign::Pad] Pad034
  BaseFeature = -> BaseBend020
  Direction = (0,-1,2e-16)
  Length = 0.3
  Length2 = 10
  Profile = -> Sketch101
  ReferenceAxis = -> Sketch101 [N_Axis]
  Reversed = true
  Suppressed = false
  Type = 0
FEATURE [Sketcher::SketchObject] Sketch102
  AttachmentSupport = -> [YZ_Plane027]
  FullyConstrained = true
  MapMode = 5
  Placement = pos=(0,0,0) rot=(0.57735,0.57735,0.57735;2.0944rad)
  expr: Constraints[14] = <<Sketch100>>.Constraints.height
  expr: Constraints[6] = <<BaseBend020>>.length
  sketch-geometry (6):
    g0: LineSegment StartX=0.5 StartY=39 StartZ=0 EndX=82.6569 EndY=39 EndZ=0
    g1: LineSegment StartX=85.3186 StartY=48.2326 StartZ=0 EndX=3 EndY=100 EndZ=0
    g2: LineSegment StartX=3 StartY=100 StartZ=0 EndX=0.5 EndY=100 EndZ=0
    g3: LineSegment StartX=0.5 StartY=100 StartZ=0 EndX=0.5 EndY=39 EndZ=0
    g4: ArcOfCircle CenterX=82.6569 CenterY=44 CenterZ=0 NormalX=0 NormalY=0 NormalZ=1 AngleXU=0 Radius=5 StartAngle=4.71239 EndAngle=7.29261
    g5: GeomPoint X=100 Y=39 Z=0
  constraints (16):
    c: Coincident(g1,g2)
    c: Horizontal(g2)
    c: Coincident(g2,g3)
    c: Coincident(g3,g0)
    c: Vertical(g3)
    c: DistanceX(g1) = 3
    c: DistanceY(g2) = 100
    c: Horizontal(g0)
    c: DistanceX(g2) = 0.5
    c: PointOnObject(g5,g0)
    c: PointOnObject(g5,g1)
    c: Tangent(g0,g4) = -1.5708
    c: Tangent(g1,g4) = -1.5708
    c: Radius(g4) = 5
    c: DistanceY(g0) = 39
    c: DistanceX(g5) = 100
FEATURE [PartDesign::Pad] Pad035
  BaseFeature = -> Pad034
  Direction = (1,0,0)
  Length = 0.3
  Length2 = 10
  Profile = -> Sketch102
  ReferenceAxis = -> Sketch102 [N_Axis]
  Reversed = true
  Suppressed = false
  Type = 0
FEATURE [PartDesign::Pocket] Pocket012
  BaseFeature = -> Pad035
  Direction = (0,1,-2e-16)
  Length = 5
  Length2 = 5
  Profile = -> Sketch100
  ReferenceAxis = -> Sketch100 [N_Axis]
  Refine = true
  Suppressed = false
  Type = 1
FEATURE [PartDesign::Boolean] Boolean021
  BaseFeature = -> Pocket012
  Group = -> [Fusion021]
  Suppressed = false
  Type = 1
  UsePlacement = true
FEATURE [PartDesign::Body] Body026  label="bottom_front_connect"
  Group = -> [Binder038,BaseBend020,Sketch100,Sketch101,Pad034,Sketch102,Pad035,Pocket012,Boolean021,Local_CS041]
  Origin = -> Origin027
  Tip = -> Pad035
COMPONENT P20 — recipe-attached ("door_fix_face", modeled in this document).
Construction recipe (the document's own serialized feature program — sketch geometry with constraints, then the solid features built on it; lengths are millimeters unless a unit is written):

FEATURE [PartDesign::SubShapeBinder] Binder039
  BindCopyOnChange = 0
  BindMode = 0
  ClaimChildren = true
  Context = -> Body027 [Binder039.]
  Fuse = false
  MakeFace = true
  OffsetFill = false
  OffsetIntersection = false
  OffsetJoinType = 0
  OffsetOpenResult = false
  PartialLoad = false
  Relative = false
  Support = -> [Sketch105]
  _Version = 2
FEATURE [PartDesign::Pad] Pad036
  Direction = (0,0,1)
  Length = 14
  Length2 = 10
  Midplane = true
  Profile = -> Binder039
  Suppressed = false
  Type = 0
FEATURE [Sketcher::SketchObject] Sketch108
  AttachmentOffset = pos=(0,0,7) rot=(0,0,1;0rad)
  AttachmentSupport = -> [XY_Plane028]
  FullyConstrained = false
  MapMode = 5
  Placement = pos=(0,0,7) rot=(0,0,1;0rad)
  sketch-geometry (4):
    g0: LineSegment StartX=429.371 StartY=245 StartZ=0 EndX=451.018 EndY=245 EndZ=0
    g1: LineSegment StartX=451.018 StartY=245 StartZ=0 EndX=451.018 EndY=282.644 EndZ=0
    g2: LineSegment StartX=451.018 StartY=282.644 StartZ=0 EndX=429.371 EndY=282.644 EndZ=0
    g3: LineSegment StartX=429.371 StartY=282.644 StartZ=0 EndX=429.371 EndY=245 EndZ=0
  constraints (9):
    c: Coincident(g0,g1)
    c: Coincident(g1,g2)
    c: Coincident(g2,g3)
    c: Coincident(g3,g0)
    c: Horizontal(g0)
    c: Horizontal(g2)
    c: Vertical(g1)
    c: Vertical(g3)
    c: DistanceY(g0) = 245
FEATURE [Sketcher::SketchObject] Sketch112
  AttachmentSupport = -> [Binder039]
  FullyConstrained = true
  MapMode = 7
  Placement = pos=(420.247,212.595,0) rot=(-0.247984,0.68502,0.68502;3.62775rad)
  sketch-geometry (3):
    g0: ArcOfCircle CenterX=-7 CenterY=0 CenterZ=0 NormalX=0 NormalY=0 NormalZ=1 AngleXU=0 Radius=7 StartAngle=0 EndAngle=1.5708
    g1: LineSegment StartX=0 StartY=0 StartZ=0 EndX=0 EndY=7 EndZ=0
    g2: LineSegment StartX=0 StartY=7 StartZ=0 EndX=-7 EndY=7 EndZ=0
  constraints (8):
    c: PointOnObject(g0,g-1)
    c: Coincident(g1,g2)
    c: Horizontal(g2)
    c: Tangent(g0,g1) = -1.5708
    c: Tangent(g2,g0) = -1.5708
    c: Vertical(g1)
    c: PointOnObject(g0,g-2)
    c: DistanceY(g1) = 7
FEATURE [PartDesign::Pocket] Pocket016
  BaseFeature = -> Pad036
  Direction = (0.64013,-0.768267,-3e-16)
  Length = 5
  Length2 = 5
  Midplane = true
  Profile = -> Sketch112
  ReferenceAxis = -> Sketch112 [N_Axis]
  Suppressed = false
  Type = 1
FEATURE [PartDesign::Mirrored] Mirrored009
  BaseFeature = -> Pocket016
  MirrorPlane = -> XY_Plane028
  Originals = -> [Pocket016]
  Suppressed = false
FEATURE [PartDesign::Boolean] Boolean023
  BaseFeature = -> Mirrored009
  Group = -> [Fusion023]
  Suppressed = false
  Type = 1
  UsePlacement = true
FEATURE [PartDesign::Body] Body027  label="door_fix_face"
  Group = -> [Binder039,Pad036,Sketch108,Pocket016,Mirrored009,Boolean023,Sketch112]
  Origin = -> Origin028
  Tip = -> Boolean023
COMPONENT P21 — recipe-attached ("door_fix_glass", modeled in this document).
Construction recipe (the document's own serialized feature program — sketch geometry with constraints, then the solid features built on it; lengths are millimeters unless a unit is written):

FEATURE [PartDesign::SubShapeBinder] Binder040
  BindCopyOnChange = 0
  BindMode = 0
  ClaimChildren = true
  Context = -> Body028 [Binder040.]
  Fuse = false
  MakeFace = true
  OffsetFill = false
  OffsetIntersection = false
  OffsetJoinType = 0
  OffsetOpenResult = false
  PartialLoad = false
  Relative = false
  Support = -> [Sketch106]
  _Version = 2
FEATURE [PartDesign::Pad] Pad037
  Direction = (0,0,1)
  Length = 33
  Length2 = 10
  Midplane = true
  Profile = -> Binder040
  Suppressed = false
  Type = 0
FEATURE [PartDesign::SubShapeBinder] Binder041
  BindCopyOnChange = 0
  BindMode = 0
  ClaimChildren = false
  Context = -> Body028 [Binder041.]
  Fuse = false
  MakeFace = true
  OffsetFill = false
  OffsetIntersection = false
  OffsetJoinType = 0
  OffsetOpenResult = false
  PartialLoad = false
  Relative = true
  Support = -> [Sketch107]
  _Version = 2
FEATURE [Sketcher::SketchObject] Sketch111
  AttachmentOffset = pos=(0,0,16.5) rot=(0,0,1;0rad)
  AttachmentSupport = -> [XY_Plane029]
  ExternalGeometry = -> [Binder041]
  FullyConstrained = true
  MapMode = 5
  Placement = pos=(0,0,16.5) rot=(0,0,1;0rad)
  sketch-geometry (1):
    g0: Circle CenterX=442.637 CenterY=246 CenterZ=0 NormalX=0 NormalY=0 NormalZ=1 AngleXU=0 Radius=3
  constraints (2):
    c: Coincident(g0,g-3)
    c: Diameter(g0) = 6
FEATURE [PartDesign::SubShapeBinder] Binder042
  BindCopyOnChange = 0
  BindMode = 0
  ClaimChildren = false
  Context = -> Body028 [Binder042.]
  Fuse = false
  MakeFace = true
  OffsetFill = false
  OffsetIntersection = false
  OffsetJoinType = 0
  OffsetOpenResult = false
  PartialLoad = false
  Relative = true
  Support = -> [Body027[Binder039.Sketch105.]]
  _Version = 2
FEATURE [Sketcher::SketchObject] Sketch109
  AttachmentSupport = -> [XY_Plane029]
  ExternalGeometry = -> [Binder042]
  FullyConstrained = true
  MapMode = 5
  sketch-geometry (4):
    g0: LineSegment StartX=447.637 StartY=230 StartZ=0 EndX=447.637 EndY=246 EndZ=0
    g1: LineSegment StartX=437.656 StartY=246.436 StartZ=0 EndX=436.218 EndY=230 EndZ=0
    g2: LineSegment StartX=436.218 StartY=230 StartZ=0 EndX=447.637 EndY=230 EndZ=0
    g3: ArcOfCircle CenterX=442.637 CenterY=246 CenterZ=0 NormalX=0 NormalY=0 NormalZ=1 AngleXU=0 Radius=5 StartAngle=9.81e-14 EndAngle=3.05433
  constraints (10):
    c: Coincident(g1,g2)
    c: Coincident(g2,g0)
    c: Vertical(g0)
    c: Horizontal(g2)
    c: DistanceY(g0) = 230
    c: Coincident(g3,g-3)
    c: Tangent(g3,g1) = -1.5708
    c: Tangent(g3,g0) = -1.5708
    c: Distance(g-3,g3) = 0.5
    c: Angle(g1) = -1.65806
FEATURE [PartDesign::Pocket] Pocket014
  BaseFeature = -> Pad037
  Direction = (0,0,-1)
  Length = 15
  Length2 = 5
  Midplane = true
  Profile = -> Sketch109
  ReferenceAxis = -> Sketch109 [N_Axis]
  Suppressed = false
  Type = 0
FEATURE [PartDesign::Pocket] Pocket015
  BaseFeature = -> Pocket014
  Direction = (0,0,-1)
  Length = 3
  Length2 = 5
  Profile = -> Sketch111
  ReferenceAxis = -> Sketch111 [N_Axis]
  Suppressed = false
  Type = 0
FEATURE [PartDesign::Boolean] Boolean024
  BaseFeature = -> Pocket015
  Group = -> [Fusion024]
  Suppressed = false
  Type = 1
  UsePlacement = true
FEATURE [PartDesign::Fillet] Fillet
  Base = -> Boolean024 [Edge26,Edge7]
  BaseFeature = -> Boolean024
  Radius = 1
  SupportTransform = false
  Suppressed = false
  UseAllEdges = false
FEATURE [PartDesign::Body] Body028  label="door_fix_glass"
  Group = -> [Binder040,Pad037,Sketch109,Pocket014,Sketch111,Pocket015,Boolean024,Binder041,Binder042,Fillet]
  Origin = -> Origin029
  Tip = -> Fillet
COMPONENT P22 — recipe-attached ("Body029", modeled in this document).
Construction recipe (the document's own serialized feature program — sketch geometry with constraints, then the solid features built on it; lengths are millimeters unless a unit is written):

FEATURE [Sketcher::SketchObject] Sketch110
  AttachmentSupport = -> [XZ_Plane030]
  FullyConstrained = true
  MapMode = 5
  Placement = pos=(0,0,0) rot=(1,0,0;1.5708rad)
  sketch-geometry (6):
    g0: LineSegment StartX=0 StartY=50 StartZ=0 EndX=5.25 EndY=50 EndZ=0
    g1: LineSegment StartX=5.25 StartY=6 StartZ=0 EndX=2.25 EndY=6 EndZ=0
    g2: LineSegment StartX=2.25 StartY=6 StartZ=0 EndX=2.25 EndY=-50 EndZ=0
    g3: LineSegment StartX=2.25 StartY=-50 StartZ=0 EndX=0 EndY=-50 EndZ=0
    g4: LineSegment StartX=0 StartY=-50 StartZ=0 EndX=0 EndY=50 EndZ=0
    g5: LineSegment StartX=5.25 StartY=6 StartZ=0 EndX=5.25 EndY=50 EndZ=0
  constraints (18):
    c: PointOnObject(g0,g-2)
    c: Horizontal(g0)
    c: Horizontal(g1)
    c: Coincident(g1,g2)
    c: Vertical(g2)
    c: Coincident(g2,g3)
    c: PointOnObject(g3,g-2)
    c: Coincident(g3,g4)
    c: Coincident(g4,g0)
    c: DistanceY(g1) = 6
    c: DistanceX(g1) = 2.25
    c: DistanceX(g1) = 5.25
    c: Coincident(g5,g1)
    c: Coincident(g5,g0)
    c: DistanceY(g0) = 50
    c: Horizontal(g3)
    c: DistanceY(g3) = -50
    c: Vertical(g5)
FEATURE [PartDesign::Revolution] Revolution
  Angle = 360
  Angle2 = 60
  Axis = (0,2e-16,1)
  Base = (0,0,0)
  Placement = pos=(0,0,0) rot=(1,0,0;1.5708rad)
  Profile = -> Sketch110
  ReferenceAxis = -> Sketch110 [V_Axis]
  Reversed = true
  Suppressed = false
  Type = 0
FEATURE [PartDesign::Body] Body029
  Group = -> [Sketch110,Revolution]
  Origin = -> Origin030
  Tip = -> Revolution
COMPONENT P23 — recipe-attached ("Body030", modeled in this document).
Construction recipe (the document's own serialized feature program — sketch geometry with constraints, then the solid features built on it; lengths are millimeters unless a unit is written):

FEATURE [PartDesign::AdditiveCylinder] Cylinder001
  Angle = 360
  AttacherType = Attacher::AttachEngine3D
  AttachmentSupport = -> [XY_Plane031]
  FirstAngle = 0
  Height = 10
  MapMode = 5
  Radius = 1.75
  SecondAngle = 0
  Suppressed = false
FEATURE [PartDesign::Body] Body030
  Group = -> [Cylinder001]
  Origin = -> Origin031
  Tip = -> Cylinder001
COMPONENT P24 — recipe-attached ("Body031", modeled in this document).
Construction recipe (the document's own serialized feature program — sketch geometry with constraints, then the solid features built on it; lengths are millimeters unless a unit is written):

FEATURE [PartDesign::AdditiveCylinder] Cylinder002
  Angle = 360
  AttacherType = Attacher::AttachEngine3D
  AttachmentOffset = pos=(0,0,-6) rot=(0,0,1;0rad)
  AttachmentSupport = -> [XY_Plane032]
  FirstAngle = 0
  Height = 10
  MapMode = 5
  Placement = pos=(0,0,-6) rot=(0,0,1;0rad)
  Radius = 2
  SecondAngle = 0
  Suppressed = false
FEATURE [PartDesign::Body] Body031
  Group = -> [Cylinder002]
  Origin = -> Origin032
  Tip = -> Cylinder002
COMPONENT P25 — recipe-attached ("door_magnet_resp", modeled in this document).
Construction recipe (the document's own serialized feature program — sketch geometry with constraints, then the solid features built on it; lengths are millimeters unless a unit is written):

FEATURE [PartDesign::SubShapeBinder] Binder043
  BindCopyOnChange = 0
  BindMode = 0
  ClaimChildren = true
  Context = -> Body032 [Binder043.]
  Fuse = false
  MakeFace = false
  OffsetFill = false
  OffsetIntersection = false
  OffsetJoinType = 0
  OffsetOpenResult = false
  PartialLoad = false
  Relative = true
  Support = -> [Sketch114]
  _Version = 2
FEATURE [PartDesign::FeaturePython] BaseBend021  # WARN: FeaturePython — macro-defined, semantics opaque (R4)
  BendSide = 0
  BendSketch = -> Binder043
  MidPlane = false
  Reverse = false
  Suppressed = false
  length = 100
  radius = 1
  thickness = 0.7
FEATURE [PartDesign::Boolean] Boolean025
  BaseFeature = -> BaseBend021
  Group = -> [Fusion025]
  Suppressed = false
  Type = 1
  UsePlacement = true
FEATURE [PartDesign::Body] Body032  label="door_magnet_resp"
  Group = -> [Binder043,BaseBend021,Boolean025]
  Origin = -> Origin033
  Tip = -> Boolean025
COMPONENT P26 — recipe-attached ("module_Body", modeled in this document).
Construction recipe (the document's own serialized feature program — sketch geometry with constraints, then the solid features built on it; lengths are millimeters unless a unit is written):

FEATURE [PartDesign::SubShapeBinder] Binder
  BindCopyOnChange = 0
  BindMode = 0
  ClaimChildren = true
  Context = -> Body [Binder.]
  Fuse = false
  MakeFace = true
  OffsetFill = false
  OffsetIntersection = false
  OffsetJoinType = 0
  OffsetOpenResult = false
  PartialLoad = false
  Relative = false
  Support = -> [Connect]
  _Version = 2
FEATURE [PartDesign::FeaturePython] BaseBend  # WARN: FeaturePython — macro-defined, semantics opaque (R4)
  BendSide = 0
  BendSketch = -> Binder
  MidPlane = false
  Reverse = false
  Suppressed = false
  length = 1163
  radius = 0.1
  thickness = 0.3
  expr: length = <<Properties>>.height
FEATURE [PartDesign::FeaturePython] Extend  # WARN: FeaturePython — macro-defined, semantics opaque (R4)
  BaseFeature = -> BaseBend
  Offset = 0.02
  Refine = true
  Suppressed = false
  UseSubtraction = false
  baseObject = -> BaseBend [Face1]
  gap1 = 0
  gap2 = 0
  length = 0
FEATURE [PartDesign::FeaturePython] Bend  # WARN: FeaturePython — macro-defined, semantics opaque (R4)
  AutoMiter = false
  BaseFeature = -> Extend
  BendType = 0
  LengthList = [0.1]
  LengthSpec = 0
  ReliefFactor = 0.7
  Suppressed = false
  UseReliefFactor = false
  angle = 90
  baseObject = -> Extend [Edge14,Edge29,Edge76,Edge58,Edge73]
  bendAList = [90]
  extend1 = 0
  extend2 = 0
  gap1 = 0
  gap2 = 0
  invert = false
  kfactor = 0.5
  length = 0.1
  maxExtendDist = 5
  minGap = 0.2
  minReliefGap = 1
  miterangle1 = 0
  miterangle2 = 0
  offset = 0
  radius = 0.1
  reliefType = 0
  reliefd = 1
  reliefw = 0.8
  sketchflip = false
  sketchinvert = false
  unfold = false
  expr: radius = BaseBend.radius
FEATURE [PartDesign::Boolean] Boolean002
  BaseFeature = -> Bend
  Group = -> [Fusion002]
  Refine = true
  Suppressed = false
  Type = 0
  UsePlacement = true
FEATURE [PartDesign::CoordinateSystem] Local_CS005  label="face_LCS"
  AttacherType = Attacher::AttachEngine3D
  AttachmentSupport = -> [XY_Plane]
  MapMode = 5
FEATURE [PartDesign::CoordinateSystem] Local_CS006  label="face_sink_LCS"
  AttacherType = Attacher::AttachEngine3D
  AttachmentOffset = pos=(0,30,148) rot=(0,0,1;0rad)
  AttachmentSupport = -> [XY_Plane]
  MapMode = 5
  Placement = pos=(0,30,148) rot=(0,0,1;0rad)
  expr: AttachmentOffset = <<sink_placement>>.Placement
FEATURE [PartDesign::CoordinateSystem] Local_CS007  label="face_dropper_fix_composit_LCS"
  AttacherType = Attacher::AttachEngine3D
  AttachmentOffset = pos=(0,30,1163.4) rot=(0,0,1;0rad)
  AttachmentSupport = -> [XY_Plane]
  MapMode = 5
  Placement = pos=(0,30,1163.4) rot=(0,0,1;0rad)
  expr: AttachmentOffset = <<top_placement>>.Placement * placement(vector(0; 0; 0.4); rotation(0; 0; 0))
FEATURE [PartDesign::CoordinateSystem] Local_CS011  label="face_bar1_LCS"
  AttacherType = Attacher::AttachEngine3D
  AttachmentOffset = pos=(0,27,278.5) rot=(0.707107,0,-0.707107;3.14159rad)
  AttachmentSupport = -> [XY_Plane]
  MapMode = 5
  Placement = pos=(0,27,278.5) rot=(0.707107,0,-0.707107;3.14159rad)
  expr: AttachmentOffset = <<bar1_placement>>.Placement
FEATURE [PartDesign::CoordinateSystem] Local_CS012  label="face_bar2_LCS"
  AttacherType = Attacher::AttachEngine3D
  AttachmentOffset = pos=(0,27,958.5) rot=(0.707107,0,-0.707107;3.14159rad)
  AttachmentSupport = -> [XY_Plane]
  MapMode = 5
  Placement = pos=(0,27,958.5) rot=(0.707107,0,-0.707107;3.14159rad)
  expr: AttachmentOffset = <<bar2_placement>>.Placement
FEATURE [PartDesign::CoordinateSystem] Local_CS014  label="face_rail1_LCS"
  AttacherType = Attacher::AttachEngine3D
  AttachmentOffset = pos=(441.137,4,23) rot=(0,-1,0;1.5708rad)
  AttachmentSupport = -> [XY_Plane]
  MapMode = 5
  Placement = pos=(441.137,4,23) rot=(0,-1,0;1.5708rad)
  expr: AttachmentOffset = <<pan_placement>>.Placement * <<rail1_placement>>.Placement
FEATURE [PartDesign::CoordinateSystem] Local_CS015  label="face_rail2_LCS"
  AttacherType = Attacher::AttachEngine3D
  AttachmentOffset = pos=(-441.137,4,23) rot=(0,1,0;1.5708rad)
  AttachmentSupport = -> [XY_Plane]
  MapMode = 5
  Placement = pos=(-441.137,4,23) rot=(0,1,0;1.5708rad)
  expr: .AttachmentOffset.Base.x = -<<face_rail1_LCS>>.Placement.Base.x
  expr: .AttachmentOffset.Base.y = <<face_rail1_LCS>>.Placement.Base.y
  expr: .AttachmentOffset.Base.z = <<face_rail1_LCS>>.Placement.Base.z
FEATURE [PartDesign::CoordinateSystem] Local_CS019  label="face_top_LCS"
  AttacherType = Attacher::AttachEngine3D
  AttachmentOffset = pos=(0,0,1163.4) rot=(0,0,1;0rad)
  AttachmentSupport = -> [XY_Plane]
  MapMode = 5
  Placement = pos=(0,0,1163.4) rot=(0,0,1;0rad)
  expr: .AttachmentOffset.Base.z = <<Properties>>.height + 0.4 mm
FEATURE [PartDesign::CoordinateSystem] Local_CS020  label="face_electric_shield_LCS"
  AttacherType = Attacher::AttachEngine3D
  AttachmentOffset = pos=(447.137,125,930) rot=(0.57735,0.57735,0.57735;2.0944rad)
  AttachmentSupport = -> [XY_Plane]
  MapMode = 5
  Placement = pos=(447.137,125,930) rot=(0.57735,0.57735,0.57735;2.0944rad)
  expr: AttachmentOffset = <<electric_shield_placement>>.Placement
FEATURE [PartDesign::CoordinateSystem] Local_CS022  label="face_door_LCS"
  AttacherType = Attacher::AttachEngine3D
  AttachmentOffset = pos=(0,30,250) rot=(0,0,1;0rad)
  AttachmentSupport = -> [XY_Plane]
  MapMode = 5
  Placement = pos=(0,30,250) rot=(0,0,1;0rad)
  expr: AttachmentOffset = <<door_placement>>.Placement
FEATURE [PartDesign::CoordinateSystem] Local_CS038  label="face_bottom_amplifier_LCS"
  AttacherType = Attacher::AttachEngine3D
  AttachmentOffset = pos=(444.137,0,0) rot=(0,0,1;0rad)
  AttachmentSupport = -> [XY_Plane]
  MapMode = 5
  Placement = pos=(444.137,0,0) rot=(0,0,1;0rad)
FEATURE [PartDesign::CoordinateSystem] Local_CS042  label="face_pan_LCS"
  AttacherType = Attacher::AttachEngine3D
  AttachmentOffset = pos=(0,10,10) rot=(0,0,1;0rad)
  AttachmentSupport = -> [XY_Plane]
  MapMode = 5
  Placement = pos=(0,10,10) rot=(0,0,1;0rad)
  expr: AttachmentOffset = <<pan_placement>>.Placement
FEATURE [PartDesign::Boolean] Boolean
  BaseFeature = -> Boolean002
  Group = -> [Fusion]
  Suppressed = false
  Type = 1
  UsePlacement = true
FEATURE [PartDesign::Boolean] Boolean010
  BaseFeature = -> Boolean
  Group = -> [Compound009]
  Refine = true
  Suppressed = false
  Type = 0
  UsePlacement = true
FEATURE [PartDesign::Body] Body  label="face"
  Group = -> [Binder,BaseBend,Extend,Bend,Boolean002,Boolean,Local_CS005,Local_CS006,Local_CS007,Local_CS011,Local_CS012,Local_CS014,Local_CS015,Boolean010,Local_CS019,Local_CS020,Local_CS022,Local_CS038,Local_CS042]
  Origin = -> Origin
  Tip = -> Boolean010
COMPONENT P27 — recipe-attached ("composit_electric_shield_fix", modeled in this document).
Construction recipe (the document's own serialized feature program — sketch geometry with constraints, then the solid features built on it; lengths are millimeters unless a unit is written):

FEATURE [PartDesign::SubShapeBinder] Binder001
  BindCopyOnChange = 0
  BindMode = 0
  ClaimChildren = true
  Context = -> Body002 [Binder001.]
  Fuse = false
  MakeFace = true
  OffsetFill = false
  OffsetIntersection = false
  OffsetJoinType = 0
  OffsetOpenResult = false
  PartialLoad = false
  Relative = true
  Support = -> [Sketch003]
  _Version = 2
FEATURE [PartDesign::SubShapeBinder] Binder002
  BindCopyOnChange = 0
  BindMode = 0
  ClaimChildren = true
  Context = -> Body002 [Binder002.]
  Fuse = false
  MakeFace = true
  OffsetFill = false
  OffsetIntersection = false
  OffsetJoinType = 0
  OffsetOpenResult = false
  PartialLoad = false
  Relative = true
  Support = -> [Sketch005]
  _Version = 2
FEATURE [Sketcher::SketchObject] Sketch006
  AttachmentSupport = -> [YZ_Plane002]
  ExternalGeometry = -> [Binder001]
  FullyConstrained = true
  MapMode = 5
  Placement = pos=(0,0,0) rot=(0.57735,0.57735,0.57735;2.0944rad)
  sketch-geometry (1):
    g0: ArcOfCircle CenterX=2.5 CenterY=3.01366 CenterZ=0 NormalX=0 NormalY=0 NormalZ=1 AngleXU=0 Radius=2.5 StartAngle=3.14159 EndAngle=4.89818
  constraints (3):
    c: Tangent(g0,g-2) = 1.5708
    c: Tangent(g0,g-3) = -1.5708
    c: Radius(g0) = 2.5
FEATURE [PartDesign::SubShapeBinder] Binder003
  BindCopyOnChange = 0
  BindMode = 0
  ClaimChildren = true
  Context = -> Body002 [Binder003.]
  Fuse = false
  MakeFace = true
  OffsetFill = false
  OffsetIntersection = false
  OffsetJoinType = 0
  OffsetOpenResult = false
  PartialLoad = false
  Relative = true
  Support = -> [Sketch001[Edge2]]
  _Version = 2
FEATURE [Sketcher::SketchObject] Sketch007
  AttachmentSupport = -> [Binder002]
  ExternalGeometry = -> [Binder001]
  FullyConstrained = true
  MapMode = 7
  Placement = pos=(165.096,4.26e-14,0) rot=(0.847578,-0.397021,-0.352117;1.8524rad)
  sketch-geometry (2):
    g0: ArcOfCircle CenterX=-2.5 CenterY=2.88397 CenterZ=0 NormalX=0 NormalY=0 NormalZ=1 AngleXU=0 Radius=2.5 StartAngle=4.56999 EndAngle=6.28319
    g1: LineSegment StartX=-2.85479 StartY=0.409277 StartZ=0 EndX=0 EndY=-2e-16 EndZ=0
  constraints (5):
    c: Tangent(g1,g0) = -1.5708
    c: Coincident(g1,g-1)
    c: Tangent(g0,g-2) = -1.5708
    c: Parallel(g1,g-3)
    c: Radius(g0) = 2.5
FEATURE [PartDesign::SubShapeBinder] Binder004
  BindCopyOnChange = 0
  BindMode = 0
  ClaimChildren = false
  Context = -> Body002 [Binder004.]
  Fuse = false
  MakeFace = true
  OffsetFill = false
  OffsetIntersection = false
  OffsetJoinType = 0
  OffsetOpenResult = false
  PartialLoad = false
  Relative = true
  _Version = 2
FEATURE [PartDesign::CoordinateSystem] Local_CS
  AttacherType = Attacher::AttachEngine3D
  AttachmentOffset = pos=(0,0,0) rot=(1,0,0;0.185787rad)
  AttachmentSupport = -> [XY_Plane002]
  MapMode = 5
  Placement = pos=(0,0,0) rot=(1,0,0;0.185787rad)
  expr: .AttachmentOffset.Rotation.Roll = <<Sketch003>>.Constraints.angle
FEATURE [Sketcher::SketchObject] Sketch008
  AttachmentSupport = -> [Local_CS]
  ExternalGeometry = -> [Binder001,Sketch006,Sketch007,Binder002]
  FullyConstrained = true
  MapMode = 5
  Placement = pos=(0,0,0) rot=(1,0,0;0.185787rad)
  sketch-geometry (4):
    g0: LineSegment StartX=-164.191 StartY=3.01366 StartZ=0 EndX=164.191 EndY=3.01366 EndZ=0
    g1: LineSegment StartX=164.191 StartY=3.01366 StartZ=0 EndX=442.677 EndY=239.115 EndZ=0
    g2: LineSegment StartX=442.677 StartY=239.115 StartZ=0 EndX=-442.677 EndY=239.115 EndZ=0
    g3: LineSegment StartX=-442.677 StartY=239.115 StartZ=0 EndX=-164.191 EndY=3.01366 EndZ=0
  constraints (13):
    c: Coincident(g0,g1)
    c: Coincident(g1,g2)
    c: Coincident(g2,g3)
    c: Coincident(g3,g0)
    c: Symmetric(g0,g0,g-2)
    c: Symmetric(g2,g1,g-2)
    c: PointOnObject(g-4,g0)
    c: PointOnObject(g-5,g1)
    c: Parallel(g1,g-6)
    c: PointOnObject(g-3,g2)
    c: DistanceX(g0,g0) = 328.382  'back'
    c: Distance(g1) = 365.1  'side'
    c: Distance(g2) = 885.354  'front'
FEATURE [Sketcher::SketchObject] Sketch009
  AttachmentSupport = -> [YZ_Plane002]
  ExternalGeometry = -> [Binder001]
  FullyConstrained = true
  MapMode = 5
  Placement = pos=(0,0,0) rot=(0.57735,0.57735,0.57735;2.0944rad)
  sketch-geometry (4):
    g0: ArcOfCircle CenterX=2.5 CenterY=3.01366 CenterZ=0 NormalX=0 NormalY=0 NormalZ=1 AngleXU=0 Radius=2.5 StartAngle=3.14159 EndAngle=4.89818
    g1: ArcOfCircle CenterX=2.5 CenterY=3.01366 CenterZ=0 NormalX=0 NormalY=0 NormalZ=1 AngleXU=0 Radius=2 StartAngle=3.14159 EndAngle=4.89818
    g2: LineSegment StartX=0 StartY=3.01366 StartZ=0 EndX=0.5 EndY=3.01366 EndZ=0
    g3: LineSegment StartX=2.9618 StartY=0.556683 StartZ=0 EndX=2.86944 EndY=1.04808 EndZ=0
  constraints (12):
    c: Coincident(g1,g0)
    c: Coincident(g2,g0)
    c: Coincident(g2,g1)
    c: Coincident(g3,g0)
    c: Coincident(g3,g1)
    c: Perpendicular(g1,g2)
    c: Perpendicular(g1,g3)
    c: Tangent(g0,g-3)
    c: Tangent(g0,g-2) = 1.5708
    c: Radius(g1) = 2
    c: Distance(g2) = 0.5
    c: Perpendicular(g-3,g3)
FEATURE [Sketcher::SketchObject] Sketch010
  AttachmentOffset = pos=(0,0,-7) rot=(0,0,1;0rad)
  AttachmentSupport = -> [Binder002,Sketch008]
  ExternalGeometry = -> [Binder001]
  FullyConstrained = true
  MapMode = 7
  Placement = pos=(171.395,5.24868,0.986513) rot=(0.847578,-0.397021,-0.352117;1.8524rad)
  expr: .AttachmentOffset.Base.z = -<<sink_cut_corner>>.Constraints.r
  sketch-geometry (4):
    g0: ArcOfCircle CenterX=-2.5 CenterY=2.88397 CenterZ=0 NormalX=0 NormalY=0 NormalZ=1 AngleXU=0 Radius=2.5 StartAngle=4.56999 EndAngle=6.28319
    g1: ArcOfCircle CenterX=-2.5 CenterY=2.88397 CenterZ=0 NormalX=0 NormalY=0 NormalZ=1 AngleXU=0 Radius=2 StartAngle=4.56999 EndAngle=6.28319
    g2: LineSegment StartX=-2.78383 StartY=0.904216 StartZ=0 EndX=-2.85479 EndY=0.409277 EndZ=0
    g3: LineSegment StartX=-0.5 StartY=2.88397 StartZ=0 EndX=0 EndY=2.88397 EndZ=0
  constraints (13):
    c: PointOnObject(g0,g-2)
    c: Coincident(g1,g0)
    c: Radius(g1) = 2
    c: Coincident(g2,g1)
    c: Coincident(g2,g0)
    c: Coincident(g3,g1)
    c: Coincident(g3,g0)
    c: Horizontal(g3)
    c: Perpendicular(g1,g3)
    c: Perpendicular(g1,g2)
    c: Tangent(g-3,g0)
    c: Distance(g2) = 0.5
    c: Perpendicular(g-3,g2)
FEATURE [PartDesign::Pad] Pad
  Direction = (0,-0.18472,0.982791)
  Length = 0.5
  Length2 = 10
  Placement = pos=(0,0,0) rot=(1,0,0;0.185787rad)
  Profile = -> Sketch008
  ReferenceAxis = -> Sketch008 [N_Axis]
  Suppressed = false
  Type = 0
FEATURE [PartDesign::Pad] Pad001
  BaseFeature = -> Pad
  Direction = (-0.762766,-0.635546,-0.119454)
  Length = 358.1
  Length2 = 10
  Placement = pos=(0,0,0) rot=(1,0,0;0.185787rad)
  Profile = -> Sketch010
  ReferenceAxis = -> Sketch010 [N_Axis]
  Reversed = true
  Suppressed = false
  Type = 0
  expr: Length = <<Sketch008>>.Constraints.side - <<sink_cut_corner>>.Constraints.r
FEATURE [PartDesign::Pad] Pad002
  BaseFeature = -> Pad001
  Direction = (1,0,0)
  Length = 314.382
  Length2 = 10
  Midplane = true
  Placement = pos=(0,0,0) rot=(1,0,0;0.185787rad)
  Profile = -> Sketch009
  ReferenceAxis = -> Sketch009 [N_Axis]
  Suppressed = false
  Type = 0
  expr: Length = <<Sketch008>>.Constraints.back - <<sink_cut_corner>>.Constraints.r * 2
FEATURE [PartDesign::SubShapeBinder] Binder005
  BindCopyOnChange = 0
  BindMode = 0
  ClaimChildren = true
  Context = -> Body002 [Binder005.]
  Fuse = false
  MakeFace = true
  OffsetFill = false
  OffsetIntersection = false
  OffsetJoinType = 0
  OffsetOpenResult = false
  PartialLoad = false
  Relative = false
  Support = -> [Part__Mirroring001]
  _Version = 2
FEATURE [PartDesign::Pad] Pad003
  BaseFeature = -> Pad002
  Direction = (0.762766,-0.635546,-0.119454)
  Length = 358.1
  Length2 = 10
  Placement = pos=(0,0,0) rot=(1,0,0;0.185787rad)
  Profile = -> Binder005
  Reversed = true
  Suppressed = false
  Type = 0
  expr: Length = Pad001.Length
FEATURE [PartDesign::SubShapeBinder] Binder006
  BindCopyOnChange = 0
  BindMode = 0
  ClaimChildren = true
  Context = -> Body002 [Binder006.]
  Fuse = false
  MakeFace = true
  OffsetFill = false
  OffsetIntersection = false
  OffsetJoinType = 0
  OffsetOpenResult = false
  PartialLoad = false
  Relative = false
  Support = -> [Part__Mirroring002]
  _Version = 2
FEATURE [Sketcher::SketchObject] Sketch013  label="sink_cut_corner"
  AttachmentSupport = -> [Local_CS]
  ExternalGeometry = -> [Sketch008]
  FullyConstrained = true
  MapMode = 5
  Placement = pos=(0,0,0) rot=(1,0,0;0.185787rad)
  sketch-geometry (3):
    g0: ArcOfCircle CenterX=164.191 CenterY=3.01366 CenterZ=0 NormalX=0 NormalY=0 NormalZ=1 AngleXU=0 Radius=7 StartAngle=0.703217 EndAngle=3.14159
    g1: LineSegment StartX=169.53 StartY=7.54039 StartZ=0 EndX=164.191 EndY=3.01366 EndZ=0
    g2: LineSegment StartX=164.191 StartY=3.01366 StartZ=0 EndX=157.191 EndY=3.01366 EndZ=0
  constraints (9):
    c: Coincident(g0,g-3)
    c: PointOnObject(g0,g-3)
    c: Horizontal(g0,g0)
    c: Coincident(g1,g2)
    c: Horizontal(g2)
    c: Equal(g2,g1)
    c: Radius(g0) = 7  'r'
    c: Coincident(g2,g0)
    c: Coincident(g1,g0)
FEATURE [Sketcher::SketchObject] Sketch039
  AttachmentOffset = pos=(0,0,0) rot=(0,0,1;1.5708rad)
  AttachmentSupport = -> [YZ_Plane002,Binder001]
  ExternalGeometry = -> [Binder001]
  FullyConstrained = true
  MapMode = 6
  Placement = pos=(2.12e-14,235,44.1693) rot=(0.57735,0.57735,0.57735;2.0944rad)
  sketch-geometry (10):
    g0: ArcOfCircle CenterX=0.36944 CenterY=-1.96558 CenterZ=0 NormalX=0 NormalY=0 NormalZ=1 AngleXU=0 Radius=2 StartAngle=1.5708 EndAngle=1.75658
    g1: ArcOfCircle CenterX=2.5 CenterY=-1.96558 CenterZ=0 NormalX=0 NormalY=0 NormalZ=1 AngleXU=0 Radius=2 StartAngle=1e-16 EndAngle=1.5708
    g2: LineSegment StartX=4.5 StartY=-1.96558 StartZ=0 EndX=4.5 EndY=-9.46558 EndZ=0
    g3: LineSegment StartX=4.5 StartY=-9.46558 StartZ=0 EndX=5 EndY=-9.46558 EndZ=0
    g4: LineSegment StartX=5 StartY=-9.46558 StartZ=0 EndX=5 EndY=-1.96558 EndZ=0
    g5: LineSegment StartX=2.5 StartY=0.0344176 StartZ=0 EndX=0.36944 EndY=0.0344176 EndZ=0
    g6: ArcOfCircle CenterX=2.5 CenterY=-1.96558 CenterZ=0 NormalX=0 NormalY=0 NormalZ=1 AngleXU=0 Radius=2.5 StartAngle=0 EndAngle=1.5708
    g7: ArcOfCircle CenterX=0.36944 CenterY=-1.96558 CenterZ=0 NormalX=0 NormalY=0 NormalZ=1 AngleXU=0 Radius=2.5 StartAngle=1.5708 EndAngle=1.75658
    g8: LineSegment StartX=0.36944 StartY=0.534418 StartZ=0 EndX=2.5 EndY=0.534418 EndZ=0
    g9: LineSegment StartX=-1e-16 StartY=0 StartZ=0 EndX=-0.0923599 EndY=0.491396 EndZ=0
  constraints (24):
    c: Tangent(g1,g2) = 1.5708
    c: Coincident(g2,g3)
    c: Horizontal(g3)
    c: Coincident(g3,g4)
    c: Tangent(g1,g5) = -1.5708
    c: Tangent(g0,g5) = -1.5708
    c: Coincident(g6,g1)
    c: Tangent(g6,g4) = -1.5708
    c: Vertical(g2)
    c: Vertical(g4)
    c: DistanceX(g3,g3) = 0.5
    c: Horizontal(g5)
    c: Tangent(g0,g-3) = 1.5708
    c: Equal(g0,g1)
    c: Radius(g0) = 2
    c: Coincident(g7,g0)
    c: Horizontal(g8)
    c: Tangent(g8,g6) = 1.5708
    c: Coincident(g9,g0)
    c: Coincident(g9,g7)
    c: Perpendicular(g7,g9)
    c: Tangent(g8,g7) = 1.5708
    c: DistanceY(g2,g6) = 10
    c: DistanceX(g0,g4) = 5
FEATURE [PartDesign::SubShapeBinder] Binder010
  BindCopyOnChange = 0
  BindMode = 0
  ClaimChildren = false
  Context = -> Body002 [Binder010.]
  Fuse = false
  MakeFace = true
  OffsetFill = false
  OffsetIntersection = false
  OffsetJoinType = 0
  OffsetOpenResult = false
  PartialLoad = false
  Relative = true
  Support = -> [Sketch040]
  _Version = 2
FEATURE [Sketcher::SketchObject] Sketch011
  AttachmentSupport = -> [XZ_Plane002]
  ExternalGeometry = -> [Sketch009,Binder003,Binder010]
  FullyConstrained = true
  MapMode = 5
  Placement = pos=(0,0,0) rot=(1,0,0;1.5708rad)
  sketch-geometry (5):
    g0: LineSegment StartX=-164.596 StartY=100 StartZ=0 EndX=-164.596 EndY=3.01366 EndZ=0
    g1: LineSegment StartX=-164.596 StartY=3.01366 StartZ=0 EndX=164.596 EndY=3.01366 EndZ=0
    g2: LineSegment StartX=164.596 StartY=3.01366 StartZ=0 EndX=164.596 EndY=100 EndZ=0
    g3: LineSegment StartX=164.596 StartY=100 StartZ=0 EndX=-164.596 EndY=100 EndZ=0
    g4: GeomPoint X=0 Y=51.5068 Z=0
  constraints (12):
    c: Coincident(g0,g1)
    c: Coincident(g1,g2)
    c: Coincident(g2,g3)
    c: Coincident(g3,g0)
    c: Vertical(g0)
    c: Vertical(g2)
    c: Horizontal(g1)
    c: Horizontal(g3)
    c: Symmetric(g2,g0,g4)
    c: PointOnObject(g4,g-2)
    c: PointOnObject(g-3,g1)
    c: Coincident(g2,g-5)
FEATURE [PartDesign::Pad] Pad004
  BaseFeature = -> Pad003
  Direction = (0,-1,2e-16)
  Length = 0.5
  Length2 = 10
  Placement = pos=(0,0,0) rot=(1,0,0;0.185787rad)
  Profile = -> Sketch011
  ReferenceAxis = -> Sketch011 [N_Axis]
  Reversed = true
  Suppressed = false
  Type = 0
FEATURE [Sketcher::SketchObject] Sketch014
  AttachmentOffset = pos=(164.191,0,0) rot=(0,0,1;0rad)
  AttachmentSupport = -> [XZ_Plane002]
  ExternalGeometry = -> [Sketch011]
  FullyConstrained = true
  MapMode = 5
  Placement = pos=(164.191,0,0) rot=(1,0,0;1.5708rad)
  expr: .AttachmentOffset.Base.x = <<Sketch008>>.Constraints.back / 2
  sketch-geometry (4):
    g0: ArcOfCircle CenterX=0 CenterY=3.01366 CenterZ=0 NormalX=0 NormalY=0 NormalZ=1 AngleXU=0 Radius=7 StartAngle=1.90373 EndAngle=3.14159
    g1: LineSegment StartX=-7 StartY=3.01366 StartZ=0 EndX=0.405024 EndY=3.01366 EndZ=0
    g2: LineSegment StartX=0.405024 StartY=3.01366 StartZ=0 EndX=0.405024 EndY=13.4096 EndZ=0
    g3: ArcOfCircle CenterX=-3.59498 CenterY=13.4096 CenterZ=0 NormalX=0 NormalY=0 NormalZ=1 AngleXU=0 Radius=4 StartAngle=5.04532 EndAngle=6.28319
  constraints (12):
    c: PointOnObject(g0,g-2)
    c: PointOnObject(g0,g-3)
    c: PointOnObject(g0,g-3)
    c: Radius(g0) = 7
    c: Horizontal(g1)
    c: Coincident(g1,g2)
    c: Vertical(g2)
    c: Tangent(g3,g2) = -1.5708
    c: Tangent(g3,g0) = 1.5708
    c: Radius(g3) = 4
    c: PointOnObject(g-3,g2)
    c: Coincident(g1,g0)
FEATURE [Sketcher::SketchObject] Sketch019  label="sink_face_cut"
  AttachmentSupport = -> [XZ_Plane002]
  ExternalGeometry = -> [Sketch011]
  FullyConstrained = true
  MapMode = 5
  Placement = pos=(0,0,0) rot=(1,0,0;1.5708rad)
  sketch-geometry (3):
    g0: ArcOfCircle CenterX=159.596 CenterY=95 CenterZ=0 NormalX=0 NormalY=0 NormalZ=1 AngleXU=0 Radius=5 StartAngle=-9e-16 EndAngle=1.5708
    g1: LineSegment StartX=164.596 StartY=95 StartZ=0 EndX=164.596 EndY=100 EndZ=0
    g2: LineSegment StartX=164.596 StartY=100 StartZ=0 EndX=159.596 EndY=100 EndZ=0
  constraints (7):
    c: Tangent(g0,g-3) = -1.5708
    c: Coincident(g0,g1)
    c: Coincident(g1,g2)
    c: Horizontal(g2)
    c: Coincident(g1,g-3)
    c: Radius(g0) = 5  'r'
    c: Tangent(g2,g0) = -1.5708
FEATURE [PartDesign::SubShapeBinder] Binder011
  BindCopyOnChange = 0
  BindMode = 0
  ClaimChildren = false
  Context = -> Body002 [Binder011.]
  Fuse = false
  MakeFace = true
  OffsetFill = false
  OffsetIntersection = false
  OffsetJoinType = 0
  OffsetOpenResult = false
  PartialLoad = false
  Relative = true
  Support = -> [Sketch041]
  _Version = 2
FEATURE [Sketcher::SketchObject] Sketch012
  AttachmentOffset = pos=(0,0,0) rot=(0,1,0;1.5708rad)
  AttachmentSupport = -> [Binder003]
  ExternalGeometry = -> [Sketch010,Binder002,Binder011]
  FullyConstrained = true
  MapMode = 7
  Placement = pos=(165.096,1.42e-14,0) rot=(0.890129,0.322235,0.322235;1.68692rad)
  sketch-geometry (4):
    g0: LineSegment StartX=0.5 StartY=2.96493 StartZ=0 EndX=366.113 EndY=46.9537 EndZ=0
    g1: LineSegment StartX=366.113 StartY=46.9537 StartZ=0 EndX=366.113 EndY=100 EndZ=0
    g2: LineSegment StartX=366.113 StartY=100 StartZ=0 EndX=0.5 EndY=100 EndZ=0
    g3: LineSegment StartX=0.5 StartY=100 StartZ=0 EndX=0.5 EndY=2.96493 EndZ=0
  constraints (10):
    c: Coincident(g0,g1)
    c: Coincident(g1,g2)
    c: Coincident(g2,g3)
    c: Coincident(g3,g0)
    c: Vertical(g1)
    c: Vertical(g3)
    c: Parallel(g0,g-4)
    c: PointOnObject(g-3,g0)
    c: Coincident(g2,g-5)
    c: Coincident(g1,g-5)
FEATURE [PartDesign::Pad] Pad005
  BaseFeature = -> Pad004
  Direction = (0.64013,-0.768267,0)
  Length = 0.5
  Length2 = 10
  Placement = pos=(0,0,0) rot=(1,0,0;0.185787rad)
  Profile = -> Sketch012
  ReferenceAxis = -> Sketch012 [N_Axis]
  Reversed = true
  Suppressed = false
  Type = 0
FEATURE [PartDesign::Pad] Pad006
  BaseFeature = -> Pad005
  Direction = (0.64013,0.768267,-2e-16)
  Length = 0.5
  Length2 = 10
  Placement = pos=(0,0,0) rot=(1,0,0;0.185787rad)
  Profile = -> Binder006
  Suppressed = false
  Type = 0
FEATURE [PartDesign::Pocket] Pocket
  BaseFeature = -> Pad006
  Direction = (0,0.18472,-0.982791)
  Length = 2
  Length2 = 5
  Placement = pos=(0,0,0) rot=(1,0,0;0.185787rad)
  Profile = -> Sketch013
  ReferenceAxis = -> Sketch013 [N_Axis]
  Reversed = true
  Suppressed = false
  Type = 0
FEATURE [PartDesign::Pocket] Pocket001
  BaseFeature = -> Pocket
  Direction = (0,1,-2e-16)
  Length = 2
  Length2 = 5
  Placement = pos=(0,0,0) rot=(1,0,0;0.185787rad)
  Profile = -> Sketch014
  ReferenceAxis = -> Sketch014 [N_Axis]
  Suppressed = false
  Type = 0
FEATURE [Sketcher::SketchObject] Sketch015
  AttachmentOffset = pos=(0,0,0) rot=(0,1,0;1.5708rad)
  AttachmentSupport = -> [Binder003]
  ExternalGeometry = -> [Sketch013,Sketch012]
  FullyConstrained = true
  MapMode = 7
  Placement = pos=(165.096,1.42e-14,0) rot=(0.890129,0.322235,0.322235;1.68692rad)
  expr: Constraints[9] = <<sink_cut_corner>>.Constraints.r
  sketch-geometry (5):
    g0: LineSegment StartX=8.15051 StartY=1.39286 StartZ=0 EndX=7.8549 EndY=3.84984 EndZ=0
    g1: ArcOfCircle CenterX=0.905024 CenterY=3.01366 CenterZ=0 NormalX=0 NormalY=0 NormalZ=1 AngleXU=0 Radius=7 StartAngle=0.11974 EndAngle=1.23786
    g2: ArcOfCircle CenterX=4.5 CenterY=13.4096 CenterZ=0 NormalX=0 NormalY=0 NormalZ=1 AngleXU=0 Radius=4 StartAngle=3.14159 EndAngle=4.37946
    g3: LineSegment StartX=0.5 StartY=2.96493 StartZ=0 EndX=0.5 EndY=13.4096 EndZ=0
    g4: LineSegment StartX=0.5 StartY=2.96493 StartZ=0 EndX=7.8549 EndY=3.84984 EndZ=0
  constraints (13):
    c: Coincident(g0,g-3)
    c: PointOnObject(g0,g-4)
    c: Perpendicular(g-4,g0)
    c: PointOnObject(g1,g-4)
    c: Coincident(g1,g0)
    c: Coincident(g3,g-4)
    c: Vertical(g3)
    c: Coincident(g4,g3)
    c: Coincident(g4,g0)
    c: Radius(g1) = 7
    c: Tangent(g2,g1) = 1.5708
    c: Tangent(g3,g2) = 1.5708
    c: Radius(g2) = 4
FEATURE [PartDesign::Pocket] Pocket002
  BaseFeature = -> Pocket001
  Direction = (-0.64013,0.768267,0)
  Length = 1
  Length2 = 5
  Placement = pos=(0,0,0) rot=(1,0,0;0.185787rad)
  Profile = -> Sketch015
  ReferenceAxis = -> Sketch015 [N_Axis]
  Suppressed = false
  Type = 0
FEATURE [Sketcher::SketchObject] Sketch020
  AttachmentSupport = -> [Sketch012]
  ExternalGeometry = -> [Sketch012]
  FullyConstrained = true
  MapMode = 2
  Placement = pos=(165.096,2.84e-14,0) rot=(0.890129,0.322235,0.322235;1.68692rad)
  expr: Constraints[12] = <<sink_face_cut>>.Constraints.r
  sketch-geometry (9):
    g0: LineSegment StartX=5.5 StartY=100 StartZ=0 EndX=0.5 EndY=100 EndZ=0
    g1: LineSegment StartX=0.5 StartY=95 StartZ=0 EndX=0.5 EndY=100 EndZ=0
    g2: LineSegment StartX=366.113 StartY=95 StartZ=0 EndX=366.113 EndY=100 EndZ=0
    g3: LineSegment StartX=361.113 StartY=100 StartZ=0 EndX=366.113 EndY=100 EndZ=0
    g4: ArcOfCircle CenterX=361.113 CenterY=95 CenterZ=0 NormalX=0 NormalY=0 NormalZ=1 AngleXU=0 Radius=5 StartAngle=-9e-16 EndAngle=1.5708
    g5: ArcOfCircle CenterX=5.5 CenterY=95 CenterZ=0 NormalX=0 NormalY=0 NormalZ=1 AngleXU=0 Radius=5 StartAngle=1.5708 EndAngle=3.14159
    g6: ArcOfCircle CenterX=363.113 CenterY=49.6144 CenterZ=0 NormalX=0 NormalY=0 NormalZ=1 AngleXU=0 Radius=3 StartAngle=4.83213 EndAngle=6.28319
    g7: LineSegment StartX=363.471 StartY=46.6359 StartZ=0 EndX=366.113 EndY=46.9537 EndZ=0
    g8: LineSegment StartX=366.113 StartY=46.9537 StartZ=0 EndX=366.113 EndY=49.6144 EndZ=0
  constraints (21):
    c: PointOnObject(g0,g-3)
    c: Coincident(g0,g-3)
    c: Coincident(g1,g0)
    c: Vertical(g1)
    c: Coincident(g2,g-3)
    c: Vertical(g2)
    c: PointOnObject(g3,g-3)
    c: Coincident(g3,g2)
    c: Tangent(g4,g2) = -1.5708
    c: Tangent(g4,g3) = 1.5708
    c: Tangent(g5,g0) = -1.5708
    c: Tangent(g5,g1) = 1.5708
    c: Radius(g5) = 5
    c: Equal(g5,g4)
    c: PointOnObject(g6,g-4)
    c: Coincident(g7,g8)
    c: Vertical(g8)
    c: Tangent(g6,g8) = -1.5708
    c: Tangent(g6,g7) = -1.5708
    c: Coincident(g7,g-4)
    c: Radius(g6) = 3
FEATURE [PartDesign::Pocket] Pocket003
  BaseFeature = -> Pocket002
  Direction = (0,1,-2e-16)
  Length = 5
  Length2 = 5
  Placement = pos=(0,0,0) rot=(1,0,0;0.185787rad)
  Profile = -> Sketch019
  ReferenceAxis = -> Sketch019 [N_Axis]
  Suppressed = false
  Type = 0
FEATURE [PartDesign::Pocket] Pocket004
  BaseFeature = -> Pocket003
  Direction = (-0.64013,0.768267,0)
  Length = 5
  Length2 = 5
  Placement = pos=(0,0,0) rot=(1,0,0;0.185787rad)
  Profile = -> Sketch020
  ReferenceAxis = -> Sketch020 [N_Axis]
  Suppressed = false
  Type = 0
FEATURE [PartDesign::Pad] Pad011
  BaseFeature = -> Pocket004
  Direction = (1,0,2e-16)
  Length = 885.354
  Length2 = 10
  Midplane = true
  Placement = pos=(0,0,0) rot=(1,0,0;0.185787rad)
  Profile = -> Sketch039
  ReferenceAxis = -> Sketch039 [N_Axis]
  Suppressed = false
  Type = 0
  expr: Length = <<Sketch008>>.Constraints.front
FEATURE [PartDesign::CoordinateSystem] Local_CS004  label="sink_LCS"
  AttacherType = Attacher::AttachEngine3D
  AttachmentSupport = -> [XY_Plane002]
  MapMode = 5
FEATURE [Sketcher::SketchObject] Sketch077
  AttachmentOffset = pos=(442.677,0,0) rot=(0,0,1;0rad)
  AttachmentSupport = -> [Sketch039]
  FullyConstrained = true
  MapMode = 7
  Placement = pos=(442.677,239.5,34.7037) rot=(1,0,0;1.5708rad)
  expr: .AttachmentOffset.Base.x = <<Pad011>>.Length / 2
  sketch-geometry (3):
    g0: ArcOfCircle CenterX=-5 CenterY=5 CenterZ=0 NormalX=0 NormalY=0 NormalZ=1 AngleXU=0 Radius=5 StartAngle=4.71239 EndAngle=6.28319
    g1: LineSegment StartX=-5 StartY=0 StartZ=0 EndX=0 EndY=0 EndZ=0
    g2: LineSegment StartX=0 StartY=0 StartZ=0 EndX=0 EndY=5 EndZ=0
  constraints (7):
    c: PointOnObject(g0,g-2)
    c: PointOnObject(g0,g-1)
    c: Coincident(g1,g2)
    c: Coincident(g1,g-1)
    c: Tangent(g0,g1) = -1.5708
    c: Tangent(g2,g0) = -1.5708
    c: Radius(g0) = 5
FEATURE [PartDesign::Pocket] Pocket011
  BaseFeature = -> Pad011
  Direction = (0,1,-2e-16)
  Length = 5
  Length2 = 5
  Midplane = true
  Placement = pos=(0,0,0) rot=(1,0,0;0.185787rad)
  Profile = -> Sketch077
  ReferenceAxis = -> Sketch077 [N_Axis]
  Suppressed = false
  Type = 1
FEATURE [PartDesign::Mirrored] Mirrored
  BaseFeature = -> Pocket011
  MirrorPlane = -> YZ_Plane002
  Originals = -> [Pocket,Pocket001,Pocket002,Pocket003,Pocket004,Pocket011]
  Placement = pos=(0,0,0) rot=(1,0,0;0.185787rad)
  Suppressed = false
FEATURE [PartDesign::CoordinateSystem] Local_CS027
  AttacherType = Attacher::AttachEngine3D
  AttachmentOffset = pos=(0,88.4512,16.6248) rot=(1,0,0;0.185787rad)
  AttachmentSupport = -> [XY_Plane002]
  MapMode = 5
  Placement = pos=(0,88.4512,16.6248) rot=(1,0,0;0.185787rad)
  expr: AttachmentOffset = <<sink_cutout_placement>>.Placement
FEATURE [PartDesign::SubShapeBinder] Binder031
  BindCopyOnChange = 0
  BindMode = 0
  ClaimChildren = true
  Context = -> Body002 [Binder031.]
  Fuse = false
  MakeFace = true
  OffsetFill = false
  OffsetIntersection = false
  OffsetJoinType = 0
  OffsetOpenResult = false
  PartialLoad = false
  Relative = false
  Support = -> [Boolean001[Fusion001.Populate054.Populate056.Populate055.]]
  _Version = 2
FEATURE [PartDesign::CoordinateSystem] Local_CS029
  AttacherType = Attacher::AttachEngine3D
  AttachmentOffset = pos=(0,0,0) rot=(0,0,1;3.14159rad)
  AttachmentSupport = -> [Binder031]
  MapMode = 6
  Placement = pos=(-1e-15,186.73,35.0968) rot=(0,-0.09276,0.995689;3.14159rad)
FEATURE [PartDesign::Body] Body002  label="sink"
  Group = -> [Binder001,Binder002,Sketch006,Binder003,Sketch007,Binder004,Local_CS,Sketch008,Sketch009,Sketch010,Pad,Pad001,Pad002,Binder005,Pad003,Sketch011,Pad004,Sketch012,Pad005,Binder006,Pad006,Sketch013,Pocket,Sketch014,Pocket001,Sketch015,Pocket002,Sketch019,Sketch020,Pocket003,Pocket004,Sketch039,Pad011,Binder010,Binder011,Local_CS004,Sketch077,Pocket011,Local_CS027,Binder031,Local_CS029,Mirrored,+1 more]
  Origin = -> Origin002
  Tip = -> Boolean001
COMPONENT P28 — geometry summary ("electric_shield_cut"; no construction recipe available for this part):
  bounding box: 315.0 x 88.0 x 10.0 mm
  tessellated surface: 12 triangles
  volume: 277200 mm^3 (100% of its bounding box)
  symmetry: 2-fold rotationally symmetric about the x axis; 2-fold rotationally symmetric about the y axis; 2-fold rotationally symmetric about the z axis; mirror-symmetric across its x mid-plane, y mid-plane, z mid-plane
COMPONENT P29 — geometry summary ("modules"; no construction recipe available for this part):
  bounding box: 970.0 x 817.4 x 234.4 mm
  tessellated surface: 593,076 triangles
  volume: 3082583 mm^3 (2% of its bounding box)
  symmetry: mirror-symmetric across its x mid-plane
PROVENANCE & LICENSES
A FreeCAD (.FCStd) document from a public repository crawl; recipes are the document's own serialized feature recipes (and, for linked parts, companion documents' recipes).
License: as declared in the source repository (recorded in the dataset sidecar).
